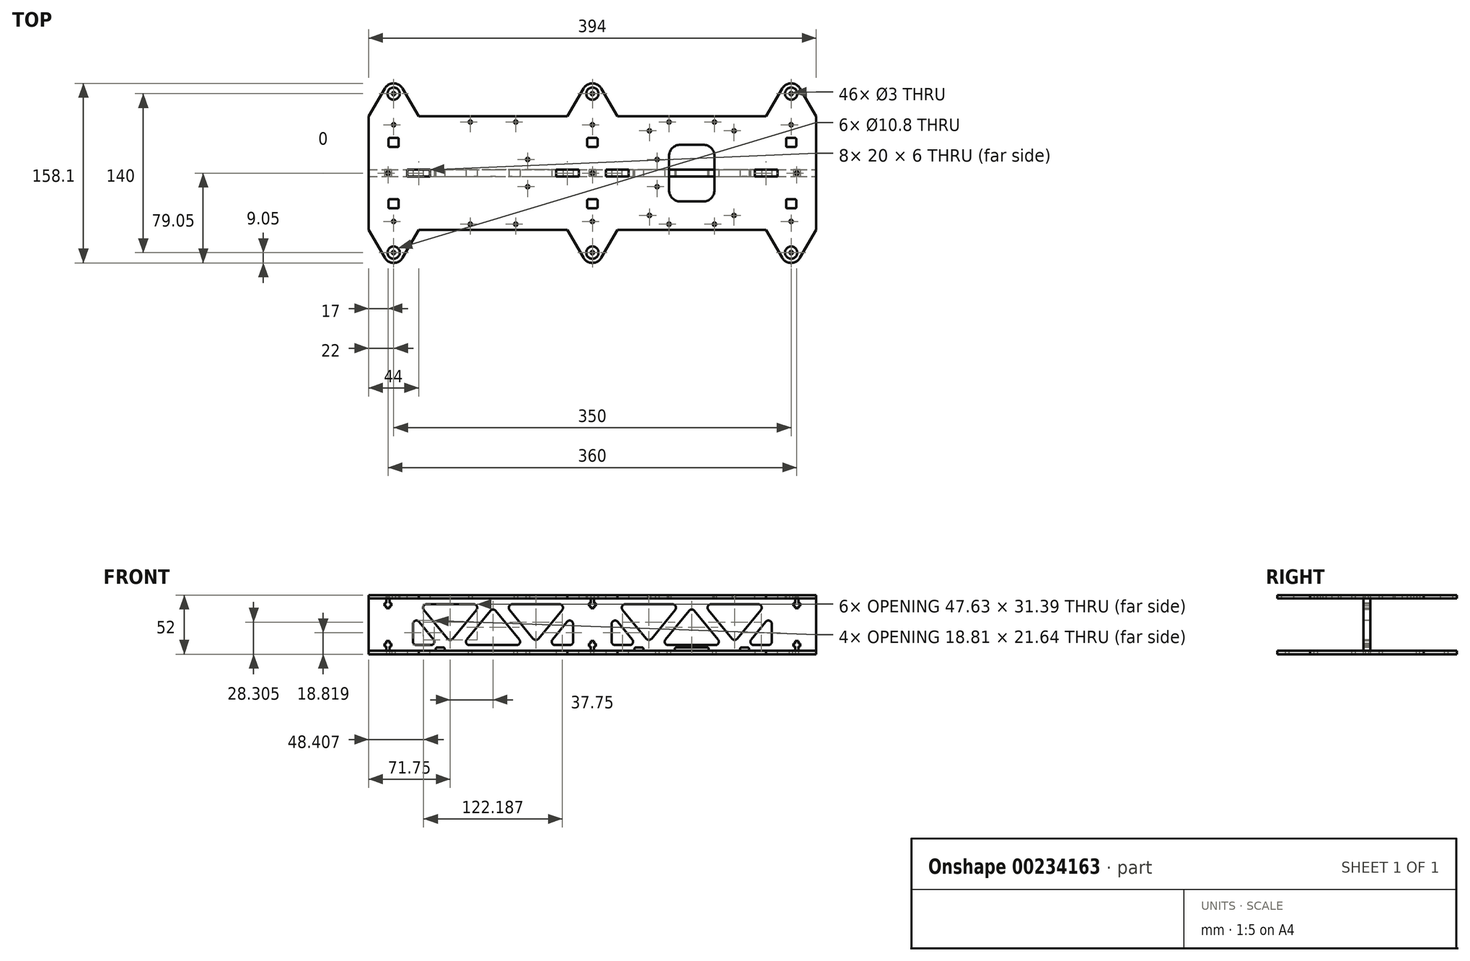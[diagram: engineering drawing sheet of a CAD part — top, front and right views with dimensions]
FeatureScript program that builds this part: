
annotation { "Feature Type Name" : "Feature", "Feature Type Description" : "" }
export const myFeature = defineFeature(function(context is Context, id is Id, definition is map)
    precondition{}
    {
        {
            assignVariable(context, id + "F0", {"name" : "MaterialThickness", "anyValue" : 3});
        }
        {
            assignVariable(context, id + "F1", {"name" : "TopBottomSeparation", "anyValue" : 46});
        }
        {
            var Q0;
            Q0=qCreatedBy(makeId("Top.planeOp"),FACE);
            var sketch = newSketch(context, id + "F2", { "sketchPlane" : qUnion([Q0])});
            skArc(sketch, "E0", {"start": v(7.84, 4.53) * mm, "mid": v(0, 9.05) * mm, "end": v(-7.84, 4.53) * mm});
            skLineSegment(sketch, "E1", {"start": v(-7.84, 4.53) * mm, "end": v(-22, -20) * mm});
            skLineSegment(sketch, "E2", {"start": v(0, 0) * mm, "end": v(0, -9.05) * mm, "construction": true});
            skLineSegment(sketch, "E3.MirrorCS", {"start": v(7.84, 4.53) * mm, "end": v(22, -20) * mm});
            skLineSegment(sketch, "E4", {"start": v(-22, -20) * mm, "end": v(-153, -20) * mm});
            skLineSegment(sketch, "E5.1.0.0", {"start": v(-167.16, 4.53) * mm, "end": v(-153, -20) * mm});
            skArc(sketch, "E5.1.0.1", {"start": v(-167.16, 4.53) * mm, "mid": v(-175, 9.05) * mm, "end": v(-182.84, 4.53) * mm});
            skLineSegment(sketch, "E5.1.0.2", {"start": v(-182.84, 4.53) * mm, "end": v(-197, -20) * mm});
            skLineSegment(sketch, "E5.2.0.0", {"start": v(-342.16, 4.53) * mm, "end": v(-328, -20) * mm});
            skArc(sketch, "E5.2.0.1", {"start": v(-342.16, 4.53) * mm, "mid": v(-350, 9.05) * mm, "end": v(-357.84, 4.53) * mm});
            skLineSegment(sketch, "E5.2.0.2", {"start": v(-357.84, 4.53) * mm, "end": v(-372, -20) * mm});
            skLineSegment(sketch, "E5.direction1", {"start": v(22, -20) * mm, "end": v(-153, -20) * mm, "construction": true});
            skLineSegment(sketch, "E6", {"start": v(-197, -20) * mm, "end": v(-328, -20) * mm});
            skLineSegment(sketch, "E7", {"start": v(22, -70) * mm, "end": v(-372, -70) * mm, "construction": true});
            skCircle(sketch, "E8", {"center": v(0, 0) * mm, "radius": 5.4 * mm});
            skCircle(sketch, "E9", {"center": v(0, -27.43) * mm, "radius": 1.5 * mm});
            skCircle(sketch, "E10.1.0.0", {"center": v(-175, 0) * mm, "radius": 5.4 * mm});
            skCircle(sketch, "E10.1.0.1", {"center": v(-175, -27.43) * mm, "radius": 1.5 * mm});
            skCircle(sketch, "E10.2.0.0", {"center": v(-350, 0) * mm, "radius": 5.4 * mm});
            skCircle(sketch, "E10.2.0.1", {"center": v(-350, -27.43) * mm, "radius": 1.5 * mm});
            skLineSegment(sketch, "E10.direction1", {"start": v(0, 0) * mm, "end": v(-175, 0) * mm, "construction": true});
            skLineSegment(sketch, "E11", {"start": v(-262.5, -70) * mm, "end": v(-262.5, -20) * mm, "construction": true});
            skLineSegment(sketch, "E12", {"start": v(-175, 0) * mm, "end": v(-175, -70) * mm, "construction": true});
            skLineSegment(sketch, "E13", {"start": v(-372, -20) * mm, "end": v(-372, -70) * mm});
            skCircle(sketch, "E14", {"center": v(-282.5, -25) * mm, "radius": 1.5 * mm});
            skCircle(sketch, "E15", {"center": v(-242.5, -25) * mm, "radius": 1.5 * mm});
            skLineSegment(sketch, "E16", {"start": v(22, -20) * mm, "end": v(22, -70) * mm});
            skCircle(sketch, "E17.MirrorC", {"center": v(-67.5, -25) * mm, "radius": 1.5 * mm});
            skCircle(sketch, "E18.MirrorC", {"center": v(-107.5, -25) * mm, "radius": 1.5 * mm});
            skLineSegment(sketch, "E19", {"start": v(0, 0) * mm, "end": v(0, -70) * mm, "construction": true});
            skLineSegment(sketch, "E20.rect.bottom", {"start": v(3.5, -47) * mm, "end": v(-3.5, -47) * mm});
            skLineSegment(sketch, "E20.rect.top", {"start": v(3.5, -39) * mm, "end": v(-3.5, -39) * mm});
            skLineSegment(sketch, "E20.rect.left", {"start": v(4.5, -46) * mm, "end": v(4.5, -40) * mm});
            skLineSegment(sketch, "E20.rect.right", {"start": v(-4.5, -46) * mm, "end": v(-4.5, -40) * mm});
            skPoint(sketch, "E20.rect.middle", {"position": v(0, -43) * mm});
            skPoint(sketch, "E21.visualSharp", {"position": v(-4.5, -39) * mm});
            skArc(sketch, "E21.filletArc", {"start": v(-3.5, -39) * mm, "mid": v(-4.2, -39.3) * mm, "end": v(-4.5, -40) * mm});
            skPoint(sketch, "E22.visualSharp", {"position": v(4.5, -39) * mm});
            skArc(sketch, "E22.filletArc", {"start": v(4.5, -40) * mm, "mid": v(4.2, -39.3) * mm, "end": v(3.5, -39) * mm});
            skPoint(sketch, "E23.visualSharp", {"position": v(-4.5, -47) * mm});
            skArc(sketch, "E23.filletArc", {"start": v(-4.5, -46) * mm, "mid": v(-4.2, -46.7) * mm, "end": v(-3.5, -47) * mm});
            skPoint(sketch, "E24.visualSharp", {"position": v(4.5, -47) * mm});
            skArc(sketch, "E24.filletArc", {"start": v(3.5, -47) * mm, "mid": v(4.2, -46.7) * mm, "end": v(4.5, -46) * mm});
            skLineSegment(sketch, "E25.1.0.0", {"start": v(-171.5, -39) * mm, "end": v(-178.5, -39) * mm});
            skPoint(sketch, "E25.1.0.1", {"position": v(-170.5, -39) * mm});
            skPoint(sketch, "E25.1.0.2", {"position": v(-175, -43) * mm});
            skLineSegment(sketch, "E25.1.0.3", {"start": v(-170.5, -46) * mm, "end": v(-170.5, -40) * mm});
            skPoint(sketch, "E25.1.0.4", {"position": v(-179.5, -47) * mm});
            skLineSegment(sketch, "E25.1.0.5", {"start": v(-171.5, -47) * mm, "end": v(-178.5, -47) * mm});
            skPoint(sketch, "E25.1.0.6", {"position": v(-170.5, -47) * mm});
            skPoint(sketch, "E25.1.0.7", {"position": v(-179.5, -39) * mm});
            skLineSegment(sketch, "E25.1.0.8", {"start": v(-179.5, -46) * mm, "end": v(-179.5, -40) * mm});
            skArc(sketch, "E25.1.0.9", {"start": v(-179.5, -46) * mm, "mid": v(-179.2, -46.7) * mm, "end": v(-178.5, -47) * mm});
            skArc(sketch, "E25.1.0.10", {"start": v(-170.5, -40) * mm, "mid": v(-170.8, -39.3) * mm, "end": v(-171.5, -39) * mm});
            skArc(sketch, "E25.1.0.11", {"start": v(-171.5, -47) * mm, "mid": v(-170.8, -46.7) * mm, "end": v(-170.5, -46) * mm});
            skArc(sketch, "E25.1.0.12", {"start": v(-178.5, -39) * mm, "mid": v(-179.2, -39.3) * mm, "end": v(-179.5, -40) * mm});
            skLineSegment(sketch, "E25.2.0.0", {"start": v(-346.5, -39) * mm, "end": v(-353.5, -39) * mm});
            skPoint(sketch, "E25.2.0.1", {"position": v(-345.5, -39) * mm});
            skPoint(sketch, "E25.2.0.2", {"position": v(-350, -43) * mm});
            skLineSegment(sketch, "E25.2.0.3", {"start": v(-345.5, -46) * mm, "end": v(-345.5, -40) * mm});
            skPoint(sketch, "E25.2.0.4", {"position": v(-354.5, -47) * mm});
            skLineSegment(sketch, "E25.2.0.5", {"start": v(-346.5, -47) * mm, "end": v(-353.5, -47) * mm});
            skPoint(sketch, "E25.2.0.6", {"position": v(-345.5, -47) * mm});
            skPoint(sketch, "E25.2.0.7", {"position": v(-354.5, -39) * mm});
            skLineSegment(sketch, "E25.2.0.8", {"start": v(-354.5, -46) * mm, "end": v(-354.5, -40) * mm});
            skArc(sketch, "E25.2.0.9", {"start": v(-354.5, -46) * mm, "mid": v(-354.2, -46.7) * mm, "end": v(-353.5, -47) * mm});
            skArc(sketch, "E25.2.0.10", {"start": v(-345.5, -40) * mm, "mid": v(-345.8, -39.3) * mm, "end": v(-346.5, -39) * mm});
            skArc(sketch, "E25.2.0.11", {"start": v(-346.5, -47) * mm, "mid": v(-345.8, -46.7) * mm, "end": v(-345.5, -46) * mm});
            skArc(sketch, "E25.2.0.12", {"start": v(-353.5, -39) * mm, "mid": v(-354.2, -39.3) * mm, "end": v(-354.5, -40) * mm});
            skLineSegment(sketch, "E25.direction1", {"start": v(-3.5, -39) * mm, "end": v(-178.5, -39) * mm, "construction": true});
            skLineSegment(sketch, "E26.MirrorCS", {"start": v(4.5, -94) * mm, "end": v(4.5, -100) * mm});
            skLineSegment(sketch, "E27.MirrorCS", {"start": v(3.5, -93) * mm, "end": v(-3.5, -93) * mm});
            skArc(sketch, "E28.MirrorCS", {"start": v(3.5, -93) * mm, "mid": v(4.2, -93.3) * mm, "end": v(4.5, -94) * mm});
            skLineSegment(sketch, "E29.MirrorCS", {"start": v(-4.5, -94) * mm, "end": v(-4.5, -100) * mm});
            skLineSegment(sketch, "E30.MirrorCS", {"start": v(-179.5, -94) * mm, "end": v(-179.5, -100) * mm});
            skLineSegment(sketch, "E31.MirrorCS", {"start": v(-171.5, -93) * mm, "end": v(-178.5, -93) * mm});
            skArc(sketch, "E32.MirrorCS", {"start": v(-179.5, -94) * mm, "mid": v(-179.2, -93.3) * mm, "end": v(-178.5, -93) * mm});
            skArc(sketch, "E33.MirrorCS", {"start": v(-171.5, -93) * mm, "mid": v(-170.8, -93.3) * mm, "end": v(-170.5, -94) * mm});
            skLineSegment(sketch, "E34.MirrorCS", {"start": v(-170.5, -94) * mm, "end": v(-170.5, -100) * mm});
            skArc(sketch, "E35.MirrorCS", {"start": v(-4.5, -94) * mm, "mid": v(-4.2, -93.3) * mm, "end": v(-3.5, -93) * mm});
            skArc(sketch, "E36.MirrorCS", {"start": v(4.5, -100) * mm, "mid": v(4.2, -100.7) * mm, "end": v(3.5, -101) * mm});
            skLineSegment(sketch, "E37.MirrorCS", {"start": v(-345.5, -94) * mm, "end": v(-345.5, -100) * mm});
            skLineSegment(sketch, "E38.MirrorCS", {"start": v(-171.5, -101) * mm, "end": v(-178.5, -101) * mm});
            skLineSegment(sketch, "E39.MirrorCS", {"start": v(3.5, -101) * mm, "end": v(-3.5, -101) * mm});
            skArc(sketch, "E40.MirrorCS", {"start": v(-178.5, -101) * mm, "mid": v(-179.2, -100.7) * mm, "end": v(-179.5, -100) * mm});
            skArc(sketch, "E41.MirrorCS", {"start": v(-3.5, -101) * mm, "mid": v(-4.2, -100.7) * mm, "end": v(-4.5, -100) * mm});
            skArc(sketch, "E42.MirrorCS", {"start": v(-170.5, -100) * mm, "mid": v(-170.8, -100.7) * mm, "end": v(-171.5, -101) * mm});
            skLineSegment(sketch, "E43.MirrorCS", {"start": v(-354.5, -94) * mm, "end": v(-354.5, -100) * mm});
            skArc(sketch, "E44.MirrorCS", {"start": v(-354.5, -94) * mm, "mid": v(-354.2, -93.3) * mm, "end": v(-353.5, -93) * mm});
            skLineSegment(sketch, "E45.MirrorCS", {"start": v(-346.5, -93) * mm, "end": v(-353.5, -93) * mm});
            skLineSegment(sketch, "E46.MirrorCS", {"start": v(-346.5, -101) * mm, "end": v(-353.5, -101) * mm});
            skArc(sketch, "E47.MirrorCS", {"start": v(-353.5, -101) * mm, "mid": v(-354.2, -100.7) * mm, "end": v(-354.5, -100) * mm});
            skArc(sketch, "E48.MirrorCS", {"start": v(-345.5, -100) * mm, "mid": v(-345.8, -100.7) * mm, "end": v(-346.5, -101) * mm});
            skCircle(sketch, "E49.MirrorC", {"center": v(-67.5, -115) * mm, "radius": 1.5 * mm});
            skCircle(sketch, "E50.MirrorC", {"center": v(-107.5, -115) * mm, "radius": 1.5 * mm});
            skCircle(sketch, "E51.MirrorC", {"center": v(0, -112.57) * mm, "radius": 1.5 * mm});
            skCircle(sketch, "E52.MirrorC", {"center": v(-282.5, -115) * mm, "radius": 1.5 * mm});
            skArc(sketch, "E53.MirrorCS", {"start": v(-342.16, -144.53) * mm, "mid": v(-350, -149.05) * mm, "end": v(-357.84, -144.53) * mm});
            skCircle(sketch, "E54.MirrorC", {"center": v(-350, -112.57) * mm, "radius": 1.5 * mm});
            skCircle(sketch, "E55.MirrorC", {"center": v(-242.5, -115) * mm, "radius": 1.5 * mm});
            skLineSegment(sketch, "E56.MirrorCS", {"start": v(0, -140) * mm, "end": v(0, -130.95) * mm, "construction": true});
            skCircle(sketch, "E57.MirrorC", {"center": v(-175, -112.57) * mm, "radius": 1.5 * mm});
            skLineSegment(sketch, "E58.MirrorCS", {"start": v(-175, -140) * mm, "end": v(-175, -70) * mm, "construction": true});
            skPoint(sketch, "E59.MirrorP", {"position": v(-179.5, -93) * mm});
            skPoint(sketch, "E60.MirrorP", {"position": v(-350, -97) * mm});
            skPoint(sketch, "E61.MirrorP", {"position": v(4.5, -93) * mm});
            skLineSegment(sketch, "E62.MirrorCS", {"start": v(-3.5, -101) * mm, "end": v(-178.5, -101) * mm, "construction": true});
            skPoint(sketch, "E63.MirrorP", {"position": v(-179.5, -101) * mm});
            skArc(sketch, "E64.MirrorCS", {"start": v(7.84, -144.53) * mm, "mid": v(0, -149.05) * mm, "end": v(-7.84, -144.53) * mm});
            skLineSegment(sketch, "E65.MirrorCS", {"start": v(-197, -120) * mm, "end": v(-328, -120) * mm});
            skPoint(sketch, "E66.MirrorP", {"position": v(-354.5, -93) * mm});
            skLineSegment(sketch, "E67.MirrorCS", {"start": v(-22, -120) * mm, "end": v(-153, -120) * mm});
            skCircle(sketch, "E68.MirrorC", {"center": v(0, -140) * mm, "radius": 5.4 * mm});
            skPoint(sketch, "E69.MirrorP", {"position": v(-4.5, -101) * mm});
            skLineSegment(sketch, "E70.MirrorCS", {"start": v(0, -140) * mm, "end": v(0, -70) * mm, "construction": true});
            skLineSegment(sketch, "E71.MirrorCS", {"start": v(-357.84, -144.53) * mm, "end": v(-372, -120) * mm});
            skLineSegment(sketch, "E72.MirrorCS", {"start": v(22, -120) * mm, "end": v(-153, -120) * mm, "construction": true});
            skCircle(sketch, "E73.MirrorC", {"center": v(-175, -140) * mm, "radius": 5.4 * mm});
            skPoint(sketch, "E74.MirrorP", {"position": v(-354.5, -101) * mm});
            skLineSegment(sketch, "E75.MirrorCS", {"start": v(7.84, -144.53) * mm, "end": v(22, -120) * mm});
            skLineSegment(sketch, "E76.MirrorCS", {"start": v(-372, -120) * mm, "end": v(-372, -70) * mm});
            skPoint(sketch, "E77.MirrorP", {"position": v(-175, -97) * mm});
            skPoint(sketch, "E78.MirrorP", {"position": v(4.5, -101) * mm});
            skArc(sketch, "E79.MirrorCS", {"start": v(-167.16, -144.53) * mm, "mid": v(-175, -149.05) * mm, "end": v(-182.84, -144.53) * mm});
            skPoint(sketch, "E80.MirrorP", {"position": v(0, -97) * mm});
            skLineSegment(sketch, "E81.MirrorCS", {"start": v(-7.84, -144.53) * mm, "end": v(-22, -120) * mm});
            skLineSegment(sketch, "E82.MirrorCS", {"start": v(-262.5, -70) * mm, "end": v(-262.5, -120) * mm, "construction": true});
            skLineSegment(sketch, "E83.MirrorCS", {"start": v(-167.16, -144.53) * mm, "end": v(-153, -120) * mm});
            skLineSegment(sketch, "E84.MirrorCS", {"start": v(-182.84, -144.53) * mm, "end": v(-197, -120) * mm});
            skLineSegment(sketch, "E85.MirrorCS", {"start": v(-342.16, -144.53) * mm, "end": v(-328, -120) * mm});
            skPoint(sketch, "E86.MirrorP", {"position": v(-170.5, -93) * mm});
            skPoint(sketch, "E87.MirrorP", {"position": v(-345.5, -93) * mm});
            skPoint(sketch, "E88.MirrorP", {"position": v(-345.5, -101) * mm});
            skPoint(sketch, "E89.MirrorP", {"position": v(-4.5, -93) * mm});
            skLineSegment(sketch, "E90.MirrorCS", {"start": v(22, -120) * mm, "end": v(22, -70) * mm});
            skPoint(sketch, "E91.MirrorP", {"position": v(-170.5, -101) * mm});
            skLineSegment(sketch, "E92.MirrorCS", {"start": v(0, -140) * mm, "end": v(-175, -140) * mm, "construction": true});
            skCircle(sketch, "E93.MirrorC", {"center": v(-350, -140) * mm, "radius": 5.4 * mm});
            skArc(sketch, "E94.MirrorCS", {"start": v(-346.5, -93) * mm, "mid": v(-345.8, -93.3) * mm, "end": v(-345.5, -94) * mm});
            skSolve(sketch);
        }
        {
            var Q0;
            Q0=makeQuery(id+"F2.imprint","IMPRINT",FACE,{"disambiguationData":[TD([[makeQuery(id+"F2.imprint","IMPRINT",EDGE,{"derivedFrom":sQuery(id+"F2.wireOp",EDGE,"E0")}),1.0]])]});
            extrude(context, id + "F3", {"entities" : qUnion([Q0]), "depth" : (getVariable(context, 'MaterialThickness')) * mm});
        }
        {
            var Q0;
            Q0=makeQuery(id+"F3.opExtrude","CAP_FACE",FACE,{"disambiguationData":[OSD([sQuery(id+"F2.wireOp",EDGE,"E0"),sQuery(id+"F2.wireOp",EDGE,"E1"),sQuery(id+"F2.wireOp",EDGE,"E3.MirrorCS"),sQuery(id+"F2.wireOp",EDGE,"E4"),sQuery(id+"F2.wireOp",EDGE,"E5.1.0.0"),sQuery(id+"F2.wireOp",EDGE,"E5.1.0.1"),sQuery(id+"F2.wireOp",EDGE,"E5.1.0.2"),sQuery(id+"F2.wireOp",EDGE,"E5.2.0.0"),sQuery(id+"F2.wireOp",EDGE,"E5.2.0.2"),sQuery(id+"F2.wireOp",EDGE,"E6"),sQuery(id+"F2.wireOp",EDGE,"E8"),sQuery(id+"F2.wireOp",EDGE,"E9"),sQuery(id+"F2.wireOp",EDGE,"E10.1.0.0"),sQuery(id+"F2.wireOp",EDGE,"E10.1.0.1"),sQuery(id+"F2.wireOp",EDGE,"E5.2.0.1"),sQuery(id+"F2.wireOp",EDGE,"E10.2.0.0"),sQuery(id+"F2.wireOp",EDGE,"E10.2.0.1"),sQuery(id+"F2.wireOp",EDGE,"E13"),sQuery(id+"F2.wireOp",EDGE,"E14"),sQuery(id+"F2.wireOp",EDGE,"E15"),sQuery(id+"F2.wireOp",EDGE,"E16"),sQuery(id+"F2.wireOp",EDGE,"E18.MirrorC"),sQuery(id+"F2.wireOp",EDGE,"E17.MirrorC"),sQuery(id+"F2.wireOp",EDGE,"E20.rect.bottom"),sQuery(id+"F2.wireOp",EDGE,"E20.rect.top"),sQuery(id+"F2.wireOp",EDGE,"E20.rect.left"),sQuery(id+"F2.wireOp",EDGE,"E20.rect.right"),sQuery(id+"F2.wireOp",EDGE,"E21.filletArc"),sQuery(id+"F2.wireOp",EDGE,"E22.filletArc"),sQuery(id+"F2.wireOp",EDGE,"E23.filletArc"),sQuery(id+"F2.wireOp",EDGE,"E24.filletArc"),sQuery(id+"F2.wireOp",EDGE,"E25.1.0.0"),sQuery(id+"F2.wireOp",EDGE,"E25.1.0.3"),sQuery(id+"F2.wireOp",EDGE,"E25.1.0.5"),sQuery(id+"F2.wireOp",EDGE,"E25.1.0.8"),sQuery(id+"F2.wireOp",EDGE,"E25.1.0.9"),sQuery(id+"F2.wireOp",EDGE,"E25.1.0.10"),sQuery(id+"F2.wireOp",EDGE,"E25.1.0.11"),sQuery(id+"F2.wireOp",EDGE,"E25.1.0.12"),sQuery(id+"F2.wireOp",EDGE,"E25.2.0.0"),sQuery(id+"F2.wireOp",EDGE,"E25.2.0.3"),sQuery(id+"F2.wireOp",EDGE,"E25.2.0.5"),sQuery(id+"F2.wireOp",EDGE,"E25.2.0.8"),sQuery(id+"F2.wireOp",EDGE,"E25.2.0.9"),sQuery(id+"F2.wireOp",EDGE,"E25.2.0.10"),sQuery(id+"F2.wireOp",EDGE,"E25.2.0.11"),sQuery(id+"F2.wireOp",EDGE,"E25.2.0.12"),sQuery(id+"F2.wireOp",EDGE,"E26.MirrorCS"),sQuery(id+"F2.wireOp",EDGE,"E27.MirrorCS"),sQuery(id+"F2.wireOp",EDGE,"E28.MirrorCS"),sQuery(id+"F2.wireOp",EDGE,"E29.MirrorCS"),sQuery(id+"F2.wireOp",EDGE,"E30.MirrorCS"),sQuery(id+"F2.wireOp",EDGE,"E31.MirrorCS"),sQuery(id+"F2.wireOp",EDGE,"E32.MirrorCS"),sQuery(id+"F2.wireOp",EDGE,"E33.MirrorCS"),sQuery(id+"F2.wireOp",EDGE,"E34.MirrorCS"),sQuery(id+"F2.wireOp",EDGE,"E35.MirrorCS"),sQuery(id+"F2.wireOp",EDGE,"E36.MirrorCS"),sQuery(id+"F2.wireOp",EDGE,"E37.MirrorCS"),sQuery(id+"F2.wireOp",EDGE,"E38.MirrorCS"),sQuery(id+"F2.wireOp",EDGE,"E39.MirrorCS"),sQuery(id+"F2.wireOp",EDGE,"E40.MirrorCS"),sQuery(id+"F2.wireOp",EDGE,"E41.MirrorCS"),sQuery(id+"F2.wireOp",EDGE,"E42.MirrorCS"),sQuery(id+"F2.wireOp",EDGE,"E43.MirrorCS"),sQuery(id+"F2.wireOp",EDGE,"E44.MirrorCS"),sQuery(id+"F2.wireOp",EDGE,"E45.MirrorCS"),sQuery(id+"F2.wireOp",EDGE,"E46.MirrorCS"),sQuery(id+"F2.wireOp",EDGE,"E47.MirrorCS"),sQuery(id+"F2.wireOp",EDGE,"E48.MirrorCS"),sQuery(id+"F2.wireOp",EDGE,"E49.MirrorC"),sQuery(id+"F2.wireOp",EDGE,"E50.MirrorC"),sQuery(id+"F2.wireOp",EDGE,"E51.MirrorC"),sQuery(id+"F2.wireOp",EDGE,"E52.MirrorC"),sQuery(id+"F2.wireOp",EDGE,"E54.MirrorC"),sQuery(id+"F2.wireOp",EDGE,"E55.MirrorC"),sQuery(id+"F2.wireOp",EDGE,"E57.MirrorC"),sQuery(id+"F2.wireOp",EDGE,"E64.MirrorCS"),sQuery(id+"F2.wireOp",EDGE,"E65.MirrorCS"),sQuery(id+"F2.wireOp",EDGE,"E67.MirrorCS"),sQuery(id+"F2.wireOp",EDGE,"E68.MirrorC"),sQuery(id+"F2.wireOp",EDGE,"E71.MirrorCS"),sQuery(id+"F2.wireOp",EDGE,"E73.MirrorC"),sQuery(id+"F2.wireOp",EDGE,"E75.MirrorCS"),sQuery(id+"F2.wireOp",EDGE,"E76.MirrorCS"),sQuery(id+"F2.wireOp",EDGE,"E79.MirrorCS"),sQuery(id+"F2.wireOp",EDGE,"E81.MirrorCS"),sQuery(id+"F2.wireOp",EDGE,"E83.MirrorCS"),sQuery(id+"F2.wireOp",EDGE,"E84.MirrorCS"),sQuery(id+"F2.wireOp",EDGE,"E53.MirrorCS"),sQuery(id+"F2.wireOp",EDGE,"E85.MirrorCS"),sQuery(id+"F2.wireOp",EDGE,"E90.MirrorCS"),sQuery(id+"F2.wireOp",EDGE,"E93.MirrorC"),sQuery(id+"F2.wireOp",EDGE,"E94.MirrorCS")])],"isStart":true});
            cPlane(context, id + "F4", {"entities" : qUnion([Q0]), "cplaneType" : CPlaneType.OFFSET, "offset" : (getVariable(context, 'TopBottomSeparation')) * mm, "width" : 150 * mm, "height" : 150 * mm});
        }
        {
            var Q0;
            Q0=qCreatedBy(id+"F4.planeOp",FACE);
            var sketch = newSketch(context, id + "F5", { "sketchPlane" : qUnion([Q0])});
            skLineSegment(sketch, "E95.0", {"start": v(-357.84, -4.53) * mm, "end": v(-357.84, -4.53) * mm});
            skLineSegment(sketch, "E96.0", {"start": v(7.84, -4.53) * mm, "end": v(22, 20) * mm});
            skLineSegment(sketch, "E97.0", {"start": v(-7.84, -4.53) * mm, "end": v(-22, 20) * mm});
            skArc(sketch, "E98.0", {"start": v(7.84, -4.53) * mm, "mid": v(0, -9.05) * mm, "end": v(-7.84, -4.53) * mm});
            skLineSegment(sketch, "E99.0", {"start": v(-22, 20) * mm, "end": v(-153, 20) * mm});
            skLineSegment(sketch, "E100.0", {"start": v(-167.16, -4.53) * mm, "end": v(-153, 20) * mm});
            skArc(sketch, "E101.0", {"start": v(-167.16, -4.53) * mm, "mid": v(-175, -9.05) * mm, "end": v(-182.84, -4.53) * mm});
            skLineSegment(sketch, "E102.0", {"start": v(-182.84, -4.53) * mm, "end": v(-197, 20) * mm});
            skLineSegment(sketch, "E103.0", {"start": v(-197, 20) * mm, "end": v(-328, 20) * mm});
            skLineSegment(sketch, "E104.0", {"start": v(-342.16, -4.53) * mm, "end": v(-328, 20) * mm});
            skArc(sketch, "E105.0", {"start": v(-342.16, -4.53) * mm, "mid": v(-350, -9.05) * mm, "end": v(-357.84, -4.53) * mm});
            skCircle(sketch, "E106", {"center": v(-350, 0) * mm, "radius": 1.5 * mm});
            skCircle(sketch, "E107.1.0.0", {"center": v(-175, 0) * mm, "radius": 1.5 * mm});
            skCircle(sketch, "E107.2.0.0", {"center": v(0, 0) * mm, "radius": 1.5 * mm});
            skLineSegment(sketch, "E107.direction1", {"start": v(-350, 0) * mm, "end": v(-175, 0) * mm, "construction": true});
            skLineSegment(sketch, "E108", {"start": v(-372, 70) * mm, "end": v(22, 70) * mm, "construction": true});
            skLineSegment(sketch, "E109.0", {"start": v(-357.84, -4.53) * mm, "end": v(-372, 20) * mm});
            skLineSegment(sketch, "E110.0", {"start": v(-372, 20) * mm, "end": v(-372, 120) * mm});
            skLineSegment(sketch, "E111.0", {"start": v(22, 120) * mm, "end": v(22, 20) * mm});
            skCircle(sketch, "E112.0", {"center": v(-282.5, 25) * mm, "radius": 1.5 * mm});
            skCircle(sketch, "E112.1", {"center": v(-242.5, 25) * mm, "radius": 1.5 * mm});
            skCircle(sketch, "E112.2", {"center": v(-107.5, 25) * mm, "radius": 1.5 * mm});
            skCircle(sketch, "E112.3", {"center": v(-67.5, 25) * mm, "radius": 1.5 * mm});
            skCircle(sketch, "E113.MirrorC", {"center": v(-350, 140) * mm, "radius": 1.5 * mm});
            skCircle(sketch, "E114.MirrorC", {"center": v(-175, 140) * mm, "radius": 1.5 * mm});
            skCircle(sketch, "E115.MirrorC", {"center": v(0, 140) * mm, "radius": 1.5 * mm});
            skCircle(sketch, "E116.MirrorC", {"center": v(-282.5, 115) * mm, "radius": 1.5 * mm});
            skCircle(sketch, "E117.MirrorC", {"center": v(-242.5, 115) * mm, "radius": 1.5 * mm});
            skCircle(sketch, "E118.MirrorC", {"center": v(-107.5, 115) * mm, "radius": 1.5 * mm});
            skCircle(sketch, "E119.MirrorC", {"center": v(-67.5, 115) * mm, "radius": 1.5 * mm});
            skArc(sketch, "E120.MirrorCS", {"start": v(-167.16, 144.53) * mm, "mid": v(-175, 149.05) * mm, "end": v(-182.84, 144.53) * mm});
            skLineSegment(sketch, "E121.MirrorCS", {"start": v(-357.84, 144.53) * mm, "end": v(-357.84, 144.53) * mm});
            skLineSegment(sketch, "E122.MirrorCS", {"start": v(-357.84, 144.53) * mm, "end": v(-372, 120) * mm});
            skLineSegment(sketch, "E123.MirrorCS", {"start": v(7.84, 144.53) * mm, "end": v(22, 120) * mm});
            skArc(sketch, "E124.MirrorCS", {"start": v(-342.16, 144.53) * mm, "mid": v(-350, 149.05) * mm, "end": v(-357.84, 144.53) * mm});
            skLineSegment(sketch, "E125.MirrorCS", {"start": v(-7.84, 144.53) * mm, "end": v(-22, 120) * mm});
            skArc(sketch, "E126.MirrorCS", {"start": v(7.84, 144.53) * mm, "mid": v(0, 149.05) * mm, "end": v(-7.84, 144.53) * mm});
            skLineSegment(sketch, "E127.MirrorCS", {"start": v(-342.16, 144.53) * mm, "end": v(-328, 120) * mm});
            skLineSegment(sketch, "E128.MirrorCS", {"start": v(-197, 120) * mm, "end": v(-328, 120) * mm});
            skLineSegment(sketch, "E129.MirrorCS", {"start": v(-182.84, 144.53) * mm, "end": v(-197, 120) * mm});
            skLineSegment(sketch, "E130.MirrorCS", {"start": v(-167.16, 144.53) * mm, "end": v(-153, 120) * mm});
            skLineSegment(sketch, "E131.MirrorCS", {"start": v(-350, 140) * mm, "end": v(-175, 140) * mm, "construction": true});
            skLineSegment(sketch, "E132.MirrorCS", {"start": v(-22, 120) * mm, "end": v(-153, 120) * mm});
            skSolve(sketch);
        }
        {
            var Q0;
            Q0=qSketchRegion(id+"F5",true);
            extrude(context, id + "F6", {"entities" : qUnion([Q0]), "depth" : (getVariable(context, 'MaterialThickness')) * mm});
        }
        {
            var Q0;
            Q0=makeQuery(id+"F3.opExtrude","CAP_FACE",FACE,{"disambiguationData":[OSD([sQuery(id+"F0T68XCoUrNjqKc_0.merge.FRI3efolS22JnH9_0.merge.F2le2PEO98lg6xs_0.merge.FXX2dDxdAnKxtOb_1.wireOp",EDGE,"a45bbf6a-1b3a-4c73-aa77-97d7b8075cbb"),sQuery(id+"F2.wireOp",EDGE,"E0"),sQuery(id+"F2.wireOp",EDGE,"E1"),sQuery(id+"F2.wireOp",EDGE,"E3.MirrorCS"),sQuery(id+"F2.wireOp",EDGE,"E4"),sQuery(id+"F2.wireOp",EDGE,"E5.1.0.0"),sQuery(id+"F2.wireOp",EDGE,"E5.1.0.1"),sQuery(id+"F2.wireOp",EDGE,"E5.1.0.2"),sQuery(id+"F2.wireOp",EDGE,"E5.2.0.0"),sQuery(id+"F2.wireOp",EDGE,"E5.2.0.2"),sQuery(id+"F2.wireOp",EDGE,"E6"),sQuery(id+"F2.wireOp",EDGE,"E9"),sQuery(id+"F2.wireOp",EDGE,"E10.1.0.0"),sQuery(id+"F2.wireOp",EDGE,"E10.1.0.1"),sQuery(id+"F2.wireOp",EDGE,"E5.2.0.1"),sQuery(id+"F2.wireOp",EDGE,"E10.2.0.0"),sQuery(id+"F2.wireOp",EDGE,"E10.2.0.1"),sQuery(id+"F2.wireOp",EDGE,"E13"),sQuery(id+"F2.wireOp",EDGE,"E14"),sQuery(id+"F2.wireOp",EDGE,"E15"),sQuery(id+"F2.wireOp",EDGE,"E16"),sQuery(id+"F2.wireOp",EDGE,"E18.MirrorC"),sQuery(id+"F2.wireOp",EDGE,"E17.MirrorC"),sQuery(id+"F2.wireOp",EDGE,"E20.rect.bottom"),sQuery(id+"F2.wireOp",EDGE,"E20.rect.top"),sQuery(id+"F2.wireOp",EDGE,"E20.rect.left"),sQuery(id+"F2.wireOp",EDGE,"E20.rect.right"),sQuery(id+"F2.wireOp",EDGE,"E21.filletArc"),sQuery(id+"F2.wireOp",EDGE,"E22.filletArc"),sQuery(id+"F2.wireOp",EDGE,"E23.filletArc"),sQuery(id+"F2.wireOp",EDGE,"E24.filletArc"),sQuery(id+"F2.wireOp",EDGE,"E25.1.0.0"),sQuery(id+"F2.wireOp",EDGE,"E25.1.0.3"),sQuery(id+"F2.wireOp",EDGE,"E25.1.0.5"),sQuery(id+"F2.wireOp",EDGE,"E25.1.0.8"),sQuery(id+"F2.wireOp",EDGE,"E25.1.0.9"),sQuery(id+"F2.wireOp",EDGE,"E25.1.0.10"),sQuery(id+"F2.wireOp",EDGE,"E25.1.0.11"),sQuery(id+"F2.wireOp",EDGE,"E25.1.0.12"),sQuery(id+"F2.wireOp",EDGE,"E25.2.0.0"),sQuery(id+"F2.wireOp",EDGE,"E25.2.0.3"),sQuery(id+"F2.wireOp",EDGE,"E25.2.0.5"),sQuery(id+"F2.wireOp",EDGE,"E25.2.0.8"),sQuery(id+"F2.wireOp",EDGE,"E25.2.0.9"),sQuery(id+"F2.wireOp",EDGE,"E25.2.0.10"),sQuery(id+"F2.wireOp",EDGE,"E25.2.0.11"),sQuery(id+"F2.wireOp",EDGE,"E25.2.0.12"),sQuery(id+"F2.wireOp",EDGE,"E26.MirrorCS"),sQuery(id+"F2.wireOp",EDGE,"E27.MirrorCS"),sQuery(id+"F2.wireOp",EDGE,"E28.MirrorCS"),sQuery(id+"F2.wireOp",EDGE,"E29.MirrorCS"),sQuery(id+"F2.wireOp",EDGE,"E30.MirrorCS"),sQuery(id+"F2.wireOp",EDGE,"E31.MirrorCS"),sQuery(id+"F2.wireOp",EDGE,"E32.MirrorCS"),sQuery(id+"F2.wireOp",EDGE,"E33.MirrorCS"),sQuery(id+"F2.wireOp",EDGE,"E34.MirrorCS"),sQuery(id+"F2.wireOp",EDGE,"E35.MirrorCS"),sQuery(id+"F2.wireOp",EDGE,"E36.MirrorCS"),sQuery(id+"F2.wireOp",EDGE,"E37.MirrorCS"),sQuery(id+"F2.wireOp",EDGE,"E38.MirrorCS"),sQuery(id+"F2.wireOp",EDGE,"E39.MirrorCS"),sQuery(id+"F2.wireOp",EDGE,"E40.MirrorCS"),sQuery(id+"F2.wireOp",EDGE,"E41.MirrorCS"),sQuery(id+"F2.wireOp",EDGE,"E42.MirrorCS"),sQuery(id+"F2.wireOp",EDGE,"E43.MirrorCS"),sQuery(id+"F2.wireOp",EDGE,"E44.MirrorCS"),sQuery(id+"F2.wireOp",EDGE,"E45.MirrorCS"),sQuery(id+"F2.wireOp",EDGE,"E46.MirrorCS"),sQuery(id+"F2.wireOp",EDGE,"E47.MirrorCS"),sQuery(id+"F2.wireOp",EDGE,"E48.MirrorCS"),sQuery(id+"F2.wireOp",EDGE,"E49.MirrorC"),sQuery(id+"F2.wireOp",EDGE,"E50.MirrorC"),sQuery(id+"F2.wireOp",EDGE,"E51.MirrorC"),sQuery(id+"F2.wireOp",EDGE,"E52.MirrorC"),sQuery(id+"F2.wireOp",EDGE,"E54.MirrorC"),sQuery(id+"F2.wireOp",EDGE,"E55.MirrorC"),sQuery(id+"F2.wireOp",EDGE,"E57.MirrorC"),sQuery(id+"F2.wireOp",EDGE,"E64.MirrorCS"),sQuery(id+"F2.wireOp",EDGE,"E65.MirrorCS"),sQuery(id+"F2.wireOp",EDGE,"E67.MirrorCS"),sQuery(id+"F2.wireOp",EDGE,"E68.MirrorC"),sQuery(id+"F2.wireOp",EDGE,"E71.MirrorCS"),sQuery(id+"F2.wireOp",EDGE,"E73.MirrorC"),sQuery(id+"F2.wireOp",EDGE,"E75.MirrorCS"),sQuery(id+"F2.wireOp",EDGE,"E76.MirrorCS"),sQuery(id+"F2.wireOp",EDGE,"E79.MirrorCS"),sQuery(id+"F2.wireOp",EDGE,"E81.MirrorCS"),sQuery(id+"F2.wireOp",EDGE,"E83.MirrorCS"),sQuery(id+"F2.wireOp",EDGE,"E84.MirrorCS"),sQuery(id+"F2.wireOp",EDGE,"E53.MirrorCS"),sQuery(id+"F2.wireOp",EDGE,"E85.MirrorCS"),sQuery(id+"F2.wireOp",EDGE,"E90.MirrorCS"),sQuery(id+"F2.wireOp",EDGE,"E93.MirrorC"),sQuery(id+"F2.wireOp",EDGE,"E94.MirrorCS")])],"isStart":false});
            var sketch = newSketch(context, id + "F7", { "sketchPlane" : qUnion([Q0])});
            skLineSegment(sketch, "E133.bottom", {"start": v(-121.75, -32.75) * mm, "end": v(-53.25, -32.75) * mm, "construction": true});
            skLineSegment(sketch, "E133.top", {"start": v(-121.75, -107.25) * mm, "end": v(-53.25, -107.25) * mm, "construction": true});
            skLineSegment(sketch, "E133.left", {"start": v(-124.75, -35.75) * mm, "end": v(-124.75, -104.25) * mm, "construction": true});
            skLineSegment(sketch, "E133.right", {"start": v(-50.25, -35.75) * mm, "end": v(-50.25, -104.25) * mm, "construction": true});
            skLineSegment(sketch, "E134", {"start": v(-124.75, -70) * mm, "end": v(-50.25, -70) * mm, "construction": true});
            skLineSegment(sketch, "E135", {"start": v(-87.5, -32.75) * mm, "end": v(-87.5, -107.25) * mm, "construction": true});
            skPoint(sketch, "E136.visualSharp", {"position": v(-124.75, -32.75) * mm});
            skArc(sketch, "E136.filletArc", {"start": v(-121.75, -32.75) * mm, "mid": v(-123.87, -33.63) * mm, "end": v(-124.75, -35.75) * mm, "construction": true});
            skPoint(sketch, "E137.visualSharp", {"position": v(-50.25, -32.75) * mm});
            skArc(sketch, "E137.filletArc", {"start": v(-50.25, -35.75) * mm, "mid": v(-51.13, -33.63) * mm, "end": v(-53.25, -32.75) * mm, "construction": true});
            skPoint(sketch, "E138.visualSharp", {"position": v(-124.75, -107.25) * mm});
            skArc(sketch, "E138.filletArc", {"start": v(-124.75, -104.25) * mm, "mid": v(-123.87, -106.37) * mm, "end": v(-121.75, -107.25) * mm, "construction": true});
            skPoint(sketch, "E139.visualSharp", {"position": v(-50.25, -107.25) * mm});
            skArc(sketch, "E139.filletArc", {"start": v(-53.25, -107.25) * mm, "mid": v(-51.13, -106.37) * mm, "end": v(-50.25, -104.25) * mm, "construction": true});
            skCircle(sketch, "E140", {"center": v(-124.75, -32.75) * mm, "radius": 1.5 * mm});
            skCircle(sketch, "E141", {"center": v(-50.25, -32.75) * mm, "radius": 1.5 * mm});
            skCircle(sketch, "E142", {"center": v(-50.25, -107.25) * mm, "radius": 1.5 * mm});
            skCircle(sketch, "E143", {"center": v(-124.75, -107.25) * mm, "radius": 1.5 * mm});
            skSolve(sketch);
        }
        {
            var Q0;
            Q0=qSketchRegion(id+"F7",true);
            extrude(context, id + "F8", {"entities" : qUnion([Q0]), "operationType" : NewBodyOperationType.REMOVE, "endBound" : BoundingType.UP_TO_NEXT, "oppositeDirection" : true, "depth" : 22.5 * mm});
        }
        {
            var Q0;
            Q0=sQuery(id+"F5.wireOp",EDGE,"E108");
            cPlane(context, id + "F9", {"entities" : qUnion([Q0]), "cplaneType" : CPlaneType.LINE_ANGLE, "offset" : 150 * mm, "angle" : 0 * degree, "width" : 150 * mm, "height" : 150 * mm});
        }
        {
            var Q0;
            Q0=qCreatedBy(id+"F9.planeOp",FACE);
            var sketch = newSketch(context, id + "F10", { "sketchPlane" : qUnion([Q0])});
            skPoint(sketch, "E144", {"position": v(372, -46) * mm});
            skPoint(sketch, "E145", {"position": v(-22, -46) * mm});
            skLineSegment(sketch, "E146", {"start": v(372, -23) * mm, "end": v(-22, -23) * mm, "construction": true});
            skLineSegment(sketch, "E147", {"start": v(372, -23) * mm, "end": v(372, -46) * mm});
            skLineSegment(sketch, "E148", {"start": v(-22, -23) * mm, "end": v(-22, -46) * mm});
            skLineSegment(sketch, "E149", {"start": v(355, -46) * mm, "end": v(355, -23) * mm, "construction": true});
            skLineSegment(sketch, "E150.top", {"start": v(353.5, -37.5) * mm, "end": v(356.5, -37.5) * mm});
            skLineSegment(sketch, "E150.left", {"start": v(353.5, -46) * mm, "end": v(353.5, -42) * mm});
            skLineSegment(sketch, "E150.right", {"start": v(356.5, -46) * mm, "end": v(356.5, -42) * mm});
            skPoint(sketch, "E150.middle", {"position": v(355, -40.75) * mm});
            skLineSegment(sketch, "E151.bottom", {"start": v(352, -42) * mm, "end": v(353.5, -42) * mm});
            skLineSegment(sketch, "E151.top", {"start": v(352, -39.5) * mm, "end": v(353.5, -39.5) * mm});
            skLineSegment(sketch, "E151.left", {"start": v(352, -42) * mm, "end": v(352, -39.5) * mm});
            skLineSegment(sketch, "E151.right", {"start": v(358, -42) * mm, "end": v(358, -39.5) * mm});
            skLineSegment(sketch, "E152.trimOffspring", {"start": v(356.5, -42) * mm, "end": v(358, -42) * mm});
            skLineSegment(sketch, "E153.trimOffspring", {"start": v(353.5, -39.5) * mm, "end": v(353.5, -37.5) * mm});
            skLineSegment(sketch, "E154.trimOffspring", {"start": v(356.5, -39.5) * mm, "end": v(358, -39.5) * mm});
            skLineSegment(sketch, "E155.trimOffspring", {"start": v(356.5, -39.5) * mm, "end": v(356.5, -37.5) * mm});
            skLineSegment(sketch, "E156", {"start": v(372, -46) * mm, "end": v(356.5, -46) * mm});
            skLineSegment(sketch, "E157", {"start": v(353.5, -46) * mm, "end": v(338, -46) * mm});
            skLineSegment(sketch, "E158.0", {"start": v(328, -49) * mm, "end": v(328, -46) * mm, "construction": true});
            skLineSegment(sketch, "E159", {"start": v(338, -46) * mm, "end": v(338, -49) * mm});
            skLineSegment(sketch, "E160", {"start": v(338, -49) * mm, "end": v(318, -49) * mm});
            skLineSegment(sketch, "E161", {"start": v(318, -49) * mm, "end": v(318, -46) * mm});
            skLineSegment(sketch, "E162.0", {"start": v(197, -49) * mm, "end": v(197, -46) * mm, "construction": true});
            skLineSegment(sketch, "E163.0", {"start": v(153, -49) * mm, "end": v(153, -46) * mm, "construction": true});
            skLineSegment(sketch, "E164.0", {"start": v(22, -49) * mm, "end": v(22, -46) * mm, "construction": true});
            skLineSegment(sketch, "E165", {"start": v(207, -46) * mm, "end": v(207, -49) * mm});
            skLineSegment(sketch, "E166", {"start": v(207, -49) * mm, "end": v(187, -49) * mm});
            skLineSegment(sketch, "E167", {"start": v(187, -49) * mm, "end": v(187, -46) * mm});
            skLineSegment(sketch, "E168", {"start": v(163, -46) * mm, "end": v(163, -49) * mm});
            skLineSegment(sketch, "E169", {"start": v(163, -49) * mm, "end": v(143, -49) * mm});
            skLineSegment(sketch, "E170", {"start": v(143, -49) * mm, "end": v(143, -46) * mm});
            skLineSegment(sketch, "E171", {"start": v(32, -46) * mm, "end": v(32, -49) * mm});
            skLineSegment(sketch, "E172", {"start": v(32, -49) * mm, "end": v(12, -49) * mm});
            skLineSegment(sketch, "E173", {"start": v(12, -49) * mm, "end": v(12, -46) * mm});
            skLineSegment(sketch, "E174.1.0.0", {"start": v(176.5, -39.5) * mm, "end": v(176.5, -37.5) * mm});
            skLineSegment(sketch, "E174.1.0.1", {"start": v(172, -42) * mm, "end": v(172, -39.5) * mm});
            skPoint(sketch, "E174.1.0.2", {"position": v(175, -40.75) * mm});
            skLineSegment(sketch, "E174.1.0.3", {"start": v(176.5, -42) * mm, "end": v(178, -42) * mm});
            skLineSegment(sketch, "E174.1.0.4", {"start": v(172, -39.5) * mm, "end": v(173.5, -39.5) * mm});
            skLineSegment(sketch, "E174.1.0.5", {"start": v(172, -42) * mm, "end": v(173.5, -42) * mm});
            skLineSegment(sketch, "E174.1.0.6", {"start": v(176.5, -46) * mm, "end": v(176.5, -42) * mm});
            skLineSegment(sketch, "E174.1.0.7", {"start": v(173.5, -37.5) * mm, "end": v(176.5, -37.5) * mm});
            skLineSegment(sketch, "E174.1.0.8", {"start": v(178, -42) * mm, "end": v(178, -39.5) * mm});
            skLineSegment(sketch, "E174.1.0.9", {"start": v(173.5, -39.5) * mm, "end": v(173.5, -37.5) * mm});
            skLineSegment(sketch, "E174.1.0.10", {"start": v(173.5, -46) * mm, "end": v(173.5, -42) * mm});
            skLineSegment(sketch, "E174.1.0.11", {"start": v(176.5, -39.5) * mm, "end": v(178, -39.5) * mm});
            skLineSegment(sketch, "E174.1.0.12", {"start": v(175, -46) * mm, "end": v(175, -23) * mm, "construction": true});
            skLineSegment(sketch, "E174.2.0.0", {"start": v(-3.5, -39.5) * mm, "end": v(-3.5, -37.5) * mm});
            skLineSegment(sketch, "E174.2.0.1", {"start": v(-8, -42) * mm, "end": v(-8, -39.5) * mm});
            skPoint(sketch, "E174.2.0.2", {"position": v(-5, -40.75) * mm});
            skLineSegment(sketch, "E174.2.0.3", {"start": v(-3.5, -42) * mm, "end": v(-2, -42) * mm});
            skLineSegment(sketch, "E174.2.0.4", {"start": v(-8, -39.5) * mm, "end": v(-6.5, -39.5) * mm});
            skLineSegment(sketch, "E174.2.0.5", {"start": v(-8, -42) * mm, "end": v(-6.5, -42) * mm});
            skLineSegment(sketch, "E174.2.0.6", {"start": v(-3.5, -46) * mm, "end": v(-3.5, -42) * mm});
            skLineSegment(sketch, "E174.2.0.7", {"start": v(-6.5, -37.5) * mm, "end": v(-3.5, -37.5) * mm});
            skLineSegment(sketch, "E174.2.0.8", {"start": v(-2, -42) * mm, "end": v(-2, -39.5) * mm});
            skLineSegment(sketch, "E174.2.0.9", {"start": v(-6.5, -39.5) * mm, "end": v(-6.5, -37.5) * mm});
            skLineSegment(sketch, "E174.2.0.10", {"start": v(-6.5, -46) * mm, "end": v(-6.5, -42) * mm});
            skLineSegment(sketch, "E174.2.0.11", {"start": v(-3.5, -39.5) * mm, "end": v(-2, -39.5) * mm});
            skLineSegment(sketch, "E174.2.0.12", {"start": v(-5, -46) * mm, "end": v(-5, -23) * mm, "construction": true});
            skLineSegment(sketch, "E174.direction1", {"start": v(353.5, -46) * mm, "end": v(313, -46) * mm, "construction": true});
            skLineSegment(sketch, "E175", {"start": v(318, -46) * mm, "end": v(313, -46) * mm});
            skLineSegment(sketch, "E176", {"start": v(187, -46) * mm, "end": v(176.5, -46) * mm});
            skLineSegment(sketch, "E177", {"start": v(173.5, -46) * mm, "end": v(163, -46) * mm});
            skLineSegment(sketch, "E178", {"start": v(143, -46) * mm, "end": v(138, -46) * mm});
            skLineSegment(sketch, "E179", {"start": v(12, -46) * mm, "end": v(-3.5, -46) * mm});
            skLineSegment(sketch, "E180", {"start": v(-6.5, -46) * mm, "end": v(-22, -46) * mm});
            skLineSegment(sketch, "E181.MirrorCS", {"start": v(172, -4) * mm, "end": v(173.5, -4) * mm});
            skLineSegment(sketch, "E182.MirrorCS", {"start": v(352, -6.5) * mm, "end": v(353.5, -6.5) * mm});
            skLineSegment(sketch, "E183.MirrorCS", {"start": v(-6.5, -6.5) * mm, "end": v(-6.5, -8.5) * mm});
            skLineSegment(sketch, "E184.MirrorCS", {"start": v(-8, -4) * mm, "end": v(-8, -6.5) * mm});
            skLineSegment(sketch, "E185.MirrorCS", {"start": v(-8, -4) * mm, "end": v(-6.5, -4) * mm});
            skLineSegment(sketch, "E186.MirrorCS", {"start": v(-3.5, -6.5) * mm, "end": v(-2, -6.5) * mm});
            skLineSegment(sketch, "E187.MirrorCS", {"start": v(173.5, 0) * mm, "end": v(173.5, -4) * mm});
            skLineSegment(sketch, "E188.MirrorCS", {"start": v(-2, -4) * mm, "end": v(-2, -6.5) * mm});
            skLineSegment(sketch, "E189.MirrorCS", {"start": v(-8, -6.5) * mm, "end": v(-6.5, -6.5) * mm});
            skLineSegment(sketch, "E190.MirrorCS", {"start": v(176.5, 0) * mm, "end": v(176.5, -4) * mm});
            skLineSegment(sketch, "E191.MirrorCS", {"start": v(172, -4) * mm, "end": v(172, -6.5) * mm});
            skLineSegment(sketch, "E192.MirrorCS", {"start": v(-6.5, -8.5) * mm, "end": v(-3.5, -8.5) * mm});
            skLineSegment(sketch, "E193.MirrorCS", {"start": v(-3.5, -4) * mm, "end": v(-2, -4) * mm});
            skLineSegment(sketch, "E194.MirrorCS", {"start": v(353.5, -8.5) * mm, "end": v(356.5, -8.5) * mm});
            skLineSegment(sketch, "E195.MirrorCS", {"start": v(353.5, -6.5) * mm, "end": v(353.5, -8.5) * mm});
            skLineSegment(sketch, "E196.MirrorCS", {"start": v(352, -4) * mm, "end": v(352, -6.5) * mm});
            skLineSegment(sketch, "E197.MirrorCS", {"start": v(176.5, -6.5) * mm, "end": v(176.5, -8.5) * mm});
            skLineSegment(sketch, "E198.MirrorCS", {"start": v(356.5, -6.5) * mm, "end": v(358, -6.5) * mm});
            skLineSegment(sketch, "E199.MirrorCS", {"start": v(-6.5, 0) * mm, "end": v(-6.5, -4) * mm});
            skLineSegment(sketch, "E200.MirrorCS", {"start": v(356.5, 0) * mm, "end": v(356.5, -4) * mm});
            skLineSegment(sketch, "E201.MirrorCS", {"start": v(353.5, 0) * mm, "end": v(353.5, -4) * mm});
            skLineSegment(sketch, "E202.MirrorCS", {"start": v(358, -4) * mm, "end": v(358, -6.5) * mm});
            skLineSegment(sketch, "E203.MirrorCS", {"start": v(176.5, -6.5) * mm, "end": v(178, -6.5) * mm});
            skLineSegment(sketch, "E204.MirrorCS", {"start": v(-3.5, -6.5) * mm, "end": v(-3.5, -8.5) * mm});
            skLineSegment(sketch, "E205.MirrorCS", {"start": v(356.5, -6.5) * mm, "end": v(356.5, -8.5) * mm});
            skLineSegment(sketch, "E206.MirrorCS", {"start": v(356.5, -4) * mm, "end": v(358, -4) * mm});
            skLineSegment(sketch, "E207.MirrorCS", {"start": v(172, -6.5) * mm, "end": v(173.5, -6.5) * mm});
            skLineSegment(sketch, "E208.MirrorCS", {"start": v(352, -4) * mm, "end": v(353.5, -4) * mm});
            skLineSegment(sketch, "E209.MirrorCS", {"start": v(176.5, -4) * mm, "end": v(178, -4) * mm});
            skLineSegment(sketch, "E210.MirrorCS", {"start": v(173.5, -8.5) * mm, "end": v(176.5, -8.5) * mm});
            skLineSegment(sketch, "E211.MirrorCS", {"start": v(178, -4) * mm, "end": v(178, -6.5) * mm});
            skLineSegment(sketch, "E212.MirrorCS", {"start": v(173.5, -6.5) * mm, "end": v(173.5, -8.5) * mm});
            skLineSegment(sketch, "E213.MirrorCS", {"start": v(143, 3) * mm, "end": v(143, 0) * mm});
            skLineSegment(sketch, "E214.MirrorCS", {"start": v(32, 0) * mm, "end": v(32, 3) * mm});
            skLineSegment(sketch, "E215.MirrorCS", {"start": v(187, 3) * mm, "end": v(187, 0) * mm});
            skLineSegment(sketch, "E216.MirrorCS", {"start": v(207, 0) * mm, "end": v(207, 3) * mm});
            skLineSegment(sketch, "E217.MirrorCS", {"start": v(187, 0) * mm, "end": v(176.5, 0) * mm});
            skLineSegment(sketch, "E218.MirrorCS", {"start": v(163, 0) * mm, "end": v(163, 3) * mm});
            skLineSegment(sketch, "E219.MirrorCS", {"start": v(338, 0) * mm, "end": v(338, 3) * mm});
            skLineSegment(sketch, "E220.MirrorCS", {"start": v(12, 3) * mm, "end": v(12, 0) * mm});
            skLineSegment(sketch, "E221.MirrorCS", {"start": v(328, 3) * mm, "end": v(328, 0) * mm, "construction": true});
            skLineSegment(sketch, "E222.MirrorCS", {"start": v(318, 3) * mm, "end": v(318, 0) * mm});
            skLineSegment(sketch, "E223.MirrorCS", {"start": v(173.5, 0) * mm, "end": v(163, 0) * mm});
            skLineSegment(sketch, "E224.MirrorCS", {"start": v(-3.5, 0) * mm, "end": v(-3.5, -4) * mm});
            skLineSegment(sketch, "E225.MirrorCS", {"start": v(353.5, 0) * mm, "end": v(338, 0) * mm});
            skLineSegment(sketch, "E226.MirrorCS", {"start": v(318, 0) * mm, "end": v(207, 0) * mm});
            skLineSegment(sketch, "E227.MirrorCS", {"start": v(153, 3) * mm, "end": v(153, 0) * mm, "construction": true});
            skLineSegment(sketch, "E228.MirrorCS", {"start": v(197, 3) * mm, "end": v(197, 0) * mm, "construction": true});
            skLineSegment(sketch, "E229.MirrorCS", {"start": v(22, 3) * mm, "end": v(22, 0) * mm, "construction": true});
            skLineSegment(sketch, "E230.MirrorCS", {"start": v(32, 3) * mm, "end": v(12, 3) * mm});
            skPoint(sketch, "E231.MirrorP", {"position": v(-5, -5.25) * mm});
            skLineSegment(sketch, "E232.MirrorCS", {"start": v(338, 3) * mm, "end": v(318, 3) * mm});
            skLineSegment(sketch, "E233.MirrorCS", {"start": v(372, -23) * mm, "end": v(372, 0) * mm});
            skLineSegment(sketch, "E234.MirrorCS", {"start": v(143, 0) * mm, "end": v(32, 0) * mm});
            skLineSegment(sketch, "E235.MirrorCS", {"start": v(355, 0) * mm, "end": v(355, -23) * mm, "construction": true});
            skPoint(sketch, "E236.MirrorP", {"position": v(355, -5.25) * mm});
            skLineSegment(sketch, "E237.MirrorCS", {"start": v(372, 0) * mm, "end": v(356.5, 0) * mm});
            skLineSegment(sketch, "E238.MirrorCS", {"start": v(-5, 0) * mm, "end": v(-5, -23) * mm, "construction": true});
            skLineSegment(sketch, "E239.MirrorCS", {"start": v(12, 0) * mm, "end": v(-3.5, 0) * mm});
            skPoint(sketch, "E240.MirrorP", {"position": v(372, 0) * mm});
            skLineSegment(sketch, "E241.MirrorCS", {"start": v(-22, -23) * mm, "end": v(-22, 0) * mm});
            skLineSegment(sketch, "E242.MirrorCS", {"start": v(-6.5, 0) * mm, "end": v(-22, 0) * mm});
            skPoint(sketch, "E243.MirrorP", {"position": v(-22, 0) * mm});
            skLineSegment(sketch, "E244.MirrorCS", {"start": v(353.5, 0) * mm, "end": v(173.5, 0) * mm, "construction": true});
            skPoint(sketch, "E245.MirrorP", {"position": v(175, -5.25) * mm});
            skLineSegment(sketch, "E246.MirrorCS", {"start": v(207, 3) * mm, "end": v(187, 3) * mm});
            skLineSegment(sketch, "E247.MirrorCS", {"start": v(163, 3) * mm, "end": v(143, 3) * mm});
            skLineSegment(sketch, "E248.MirrorCS", {"start": v(175, 0) * mm, "end": v(175, -23) * mm, "construction": true});
            skLineSegment(sketch, "E249", {"start": v(138, -46) * mm, "end": v(138, -44.5) * mm});
            skLineSegment(sketch, "E250", {"start": v(136.5, -43) * mm, "end": v(131.5, -43) * mm});
            skLineSegment(sketch, "E251", {"start": v(130, -44.5) * mm, "end": v(130, -46) * mm});
            skLineSegment(sketch, "E252.trimOffspring", {"start": v(130, -46) * mm, "end": v(102.5, -46) * mm});
            skPoint(sketch, "E253.visualSharp", {"position": v(130, -43) * mm});
            skArc(sketch, "E253.filletArc", {"start": v(131.5, -43) * mm, "mid": v(130.44, -43.44) * mm, "end": v(130, -44.5) * mm});
            skPoint(sketch, "E254.visualSharp", {"position": v(138, -43) * mm});
            skArc(sketch, "E254.filletArc", {"start": v(138, -44.5) * mm, "mid": v(137.56, -43.44) * mm, "end": v(136.5, -43) * mm});
            skLineSegment(sketch, "E255", {"start": v(37, -46) * mm, "end": v(37, -44.5) * mm});
            skLineSegment(sketch, "E256", {"start": v(38.5, -43) * mm, "end": v(43.5, -43) * mm});
            skLineSegment(sketch, "E257", {"start": v(45, -44.5) * mm, "end": v(45, -46) * mm});
            skLineSegment(sketch, "E258.trimOffspring", {"start": v(37, -46) * mm, "end": v(32, -46) * mm});
            skPoint(sketch, "E259.visualSharp", {"position": v(45, -43) * mm});
            skArc(sketch, "E259.filletArc", {"start": v(45, -44.5) * mm, "mid": v(44.56, -43.44) * mm, "end": v(43.5, -43) * mm});
            skPoint(sketch, "E260.visualSharp", {"position": v(37, -43) * mm});
            skArc(sketch, "E260.filletArc", {"start": v(38.5, -43) * mm, "mid": v(37.44, -43.44) * mm, "end": v(37, -44.5) * mm});
            skLineSegment(sketch, "E261", {"start": v(313, -46) * mm, "end": v(313, -44.5) * mm});
            skLineSegment(sketch, "E262", {"start": v(311.5, -43) * mm, "end": v(306.5, -43) * mm});
            skLineSegment(sketch, "E263", {"start": v(305, -44.5) * mm, "end": v(305, -46) * mm});
            skPoint(sketch, "E264.visualSharp", {"position": v(305, -43) * mm});
            skArc(sketch, "E264.filletArc", {"start": v(306.5, -43) * mm, "mid": v(305.44, -43.44) * mm, "end": v(305, -44.5) * mm});
            skPoint(sketch, "E265.visualSharp", {"position": v(313, -43) * mm});
            skArc(sketch, "E265.filletArc", {"start": v(313, -44.5) * mm, "mid": v(312.56, -43.44) * mm, "end": v(311.5, -43) * mm});
            skLineSegment(sketch, "E266.trimOffspring", {"start": v(305, -46) * mm, "end": v(173.5, -46) * mm, "construction": true});
            skLineSegment(sketch, "E267.trimOffspring", {"start": v(305, -46) * mm, "end": v(207, -46) * mm});
            skLineSegment(sketch, "E268", {"start": v(87.5, -46) * mm, "end": v(87.5, -23) * mm, "construction": true});
            skLineSegment(sketch, "E269", {"start": v(102.5, -46) * mm, "end": v(102.5, -44.5) * mm});
            skLineSegment(sketch, "E270", {"start": v(101, -43) * mm, "end": v(74, -43) * mm});
            skLineSegment(sketch, "E271", {"start": v(72.5, -44.5) * mm, "end": v(72.5, -46) * mm});
            skPoint(sketch, "E272", {"position": v(87.5, -43) * mm});
            skLineSegment(sketch, "E273.trimOffspring", {"start": v(72.5, -46) * mm, "end": v(45, -46) * mm});
            skPoint(sketch, "E274.visualSharp", {"position": v(102.5, -43) * mm});
            skArc(sketch, "E274.filletArc", {"start": v(102.5, -44.5) * mm, "mid": v(102.06, -43.44) * mm, "end": v(101, -43) * mm});
            skPoint(sketch, "E275.visualSharp", {"position": v(72.5, -43) * mm});
            skArc(sketch, "E275.filletArc", {"start": v(74, -43) * mm, "mid": v(72.94, -43.44) * mm, "end": v(72.5, -44.5) * mm});
            skSolve(sketch);
        }
        {
            var Q0;
            Q0=makeQuery(id+"F10.imprint","IMPRINT",FACE,{"disambiguationData":[TD([[makeQuery(id+"F10.imprint","IMPRINT",EDGE,{"derivedFrom":sQuery(id+"F10.wireOp",EDGE,"E147")}),-1.0]])]});
            extrude(context, id + "F11", {"entities" : qUnion([Q0]), "depth" : 6 * mm, "symmetric" : true});
        }
        {
            var Q0;
            Q0=makeQuery(id+"F11.opExtrude","SWEPT_BODY",BODY,{"disambiguationData":[OSD([sQuery(id+"F10.wireOp",EDGE,"E147"),sQuery(id+"F10.wireOp",EDGE,"E148"),sQuery(id+"F10.wireOp",EDGE,"KtgLcZro-Gi18-2paL-ronS-uR46lsXsDt71.bottom"),sQuery(id+"F10.wireOp",EDGE,"KtgLcZro-Gi18-2paL-ronS-uR46lsXsDt71.left"),sQuery(id+"F10.wireOp",EDGE,"KtgLcZro-Gi18-2paL-ronS-uR46lsXsDt71.right"),sQuery(id+"F10.wireOp",EDGE,"GIBqVv8B-Go3L-kjrv-fow0-1hPMpe5xOsCY.bottom"),sQuery(id+"F10.wireOp",EDGE,"GIBqVv8B-Go3L-kjrv-fow0-1hPMpe5xOsCY.left"),sQuery(id+"F10.wireOp",EDGE,"GIBqVv8B-Go3L-kjrv-fow0-1hPMpe5xOsCY.right"),sQuery(id+"F10.wireOp",EDGE,"C6l01rvX-xXIv-Yw3v-4MLj-VURo6Fi3yfat"),sQuery(id+"F10.wireOp",EDGE,"SJWZGjJp-2Uf8-EYLt-dNml-pFZFEXsSqGbw.bottom"),sQuery(id+"F10.wireOp",EDGE,"SJWZGjJp-2Uf8-EYLt-dNml-pFZFEXsSqGbw.left"),sQuery(id+"F10.wireOp",EDGE,"SJWZGjJp-2Uf8-EYLt-dNml-pFZFEXsSqGbw.right"),sQuery(id+"F10.wireOp",EDGE,"0VWDFySL-sPqn-z3Gb-qFFI-h3bUQO7hZhO1.bottom"),sQuery(id+"F10.wireOp",EDGE,"0VWDFySL-sPqn-z3Gb-qFFI-h3bUQO7hZhO1.left"),sQuery(id+"F10.wireOp",EDGE,"0VWDFySL-sPqn-z3Gb-qFFI-h3bUQO7hZhO1.right"),sQuery(id+"F10.wireOp",EDGE,"E150.top"),sQuery(id+"F10.wireOp",EDGE,"E150.left"),sQuery(id+"F10.wireOp",EDGE,"E150.right"),sQuery(id+"F10.wireOp",EDGE,"E151.bottom"),sQuery(id+"F10.wireOp",EDGE,"E151.top"),sQuery(id+"F10.wireOp",EDGE,"E151.left"),sQuery(id+"F10.wireOp",EDGE,"E151.right"),sQuery(id+"F10.wireOp",EDGE,"E152.trimOffspring"),sQuery(id+"F10.wireOp",EDGE,"E153.trimOffspring"),sQuery(id+"F10.wireOp",EDGE,"E154.trimOffspring"),sQuery(id+"F10.wireOp",EDGE,"E155.trimOffspring"),sQuery(id+"F10.wireOp",EDGE,"e2a2db74-9ea7-42a8-bf58-83d2eb57d682.trimOffspring"),sQuery(id+"F10.wireOp",EDGE,"34e65598-81c8-4b1d-b155-a18f7778bf65.1.0.0"),sQuery(id+"F10.wireOp",EDGE,"34e65598-81c8-4b1d-b155-a18f7778bf65.1.0.1"),sQuery(id+"F10.wireOp",EDGE,"34e65598-81c8-4b1d-b155-a18f7778bf65.1.0.2"),sQuery(id+"F10.wireOp",EDGE,"34e65598-81c8-4b1d-b155-a18f7778bf65.1.0.3"),sQuery(id+"F10.wireOp",EDGE,"34e65598-81c8-4b1d-b155-a18f7778bf65.1.0.4"),sQuery(id+"F10.wireOp",EDGE,"34e65598-81c8-4b1d-b155-a18f7778bf65.1.0.5"),sQuery(id+"F10.wireOp",EDGE,"34e65598-81c8-4b1d-b155-a18f7778bf65.1.0.6"),sQuery(id+"F10.wireOp",EDGE,"34e65598-81c8-4b1d-b155-a18f7778bf65.1.0.9"),sQuery(id+"F10.wireOp",EDGE,"34e65598-81c8-4b1d-b155-a18f7778bf65.1.0.10"),sQuery(id+"F10.wireOp",EDGE,"34e65598-81c8-4b1d-b155-a18f7778bf65.1.0.11"),sQuery(id+"F10.wireOp",EDGE,"34e65598-81c8-4b1d-b155-a18f7778bf65.1.0.12"),sQuery(id+"F10.wireOp",EDGE,"34e65598-81c8-4b1d-b155-a18f7778bf65.2.0.0"),sQuery(id+"F10.wireOp",EDGE,"34e65598-81c8-4b1d-b155-a18f7778bf65.2.0.1"),sQuery(id+"F10.wireOp",EDGE,"34e65598-81c8-4b1d-b155-a18f7778bf65.2.0.2"),sQuery(id+"F10.wireOp",EDGE,"34e65598-81c8-4b1d-b155-a18f7778bf65.2.0.3"),sQuery(id+"F10.wireOp",EDGE,"34e65598-81c8-4b1d-b155-a18f7778bf65.2.0.4"),sQuery(id+"F10.wireOp",EDGE,"34e65598-81c8-4b1d-b155-a18f7778bf65.2.0.5"),sQuery(id+"F10.wireOp",EDGE,"34e65598-81c8-4b1d-b155-a18f7778bf65.2.0.6"),sQuery(id+"F10.wireOp",EDGE,"34e65598-81c8-4b1d-b155-a18f7778bf65.2.0.9"),sQuery(id+"F10.wireOp",EDGE,"34e65598-81c8-4b1d-b155-a18f7778bf65.2.0.10"),sQuery(id+"F10.wireOp",EDGE,"34e65598-81c8-4b1d-b155-a18f7778bf65.2.0.11"),sQuery(id+"F10.wireOp",EDGE,"34e65598-81c8-4b1d-b155-a18f7778bf65.2.0.12"),sQuery(id+"F10.wireOp",EDGE,"34e65598-81c8-4b1d-b155-a18f7778bf65.3.0.0"),sQuery(id+"F10.wireOp",EDGE,"34e65598-81c8-4b1d-b155-a18f7778bf65.3.0.1"),sQuery(id+"F10.wireOp",EDGE,"34e65598-81c8-4b1d-b155-a18f7778bf65.3.0.2"),sQuery(id+"F10.wireOp",EDGE,"34e65598-81c8-4b1d-b155-a18f7778bf65.3.0.3"),sQuery(id+"F10.wireOp",EDGE,"34e65598-81c8-4b1d-b155-a18f7778bf65.3.0.4"),sQuery(id+"F10.wireOp",EDGE,"34e65598-81c8-4b1d-b155-a18f7778bf65.3.0.5"),sQuery(id+"F10.wireOp",EDGE,"34e65598-81c8-4b1d-b155-a18f7778bf65.3.0.6"),sQuery(id+"F10.wireOp",EDGE,"34e65598-81c8-4b1d-b155-a18f7778bf65.3.0.9"),sQuery(id+"F10.wireOp",EDGE,"34e65598-81c8-4b1d-b155-a18f7778bf65.3.0.10"),sQuery(id+"F10.wireOp",EDGE,"34e65598-81c8-4b1d-b155-a18f7778bf65.3.0.11"),sQuery(id+"F10.wireOp",EDGE,"34e65598-81c8-4b1d-b155-a18f7778bf65.3.0.12"),sQuery(id+"F10.wireOp",EDGE,"34e65598-81c8-4b1d-b155-a18f7778bf65.4.0.0"),sQuery(id+"F10.wireOp",EDGE,"34e65598-81c8-4b1d-b155-a18f7778bf65.4.0.1"),sQuery(id+"F10.wireOp",EDGE,"34e65598-81c8-4b1d-b155-a18f7778bf65.4.0.2"),sQuery(id+"F10.wireOp",EDGE,"34e65598-81c8-4b1d-b155-a18f7778bf65.4.0.3"),sQuery(id+"F10.wireOp",EDGE,"34e65598-81c8-4b1d-b155-a18f7778bf65.4.0.4"),sQuery(id+"F10.wireOp",EDGE,"34e65598-81c8-4b1d-b155-a18f7778bf65.4.0.5"),sQuery(id+"F10.wireOp",EDGE,"34e65598-81c8-4b1d-b155-a18f7778bf65.4.0.6"),sQuery(id+"F10.wireOp",EDGE,"34e65598-81c8-4b1d-b155-a18f7778bf65.4.0.9"),sQuery(id+"F10.wireOp",EDGE,"34e65598-81c8-4b1d-b155-a18f7778bf65.4.0.10"),sQuery(id+"F10.wireOp",EDGE,"34e65598-81c8-4b1d-b155-a18f7778bf65.4.0.11"),sQuery(id+"F10.wireOp",EDGE,"34e65598-81c8-4b1d-b155-a18f7778bf65.4.0.12"),sQuery(id+"F10.wireOp",EDGE,"AtrAxSzi-Mmhj-RrMe-m420-yhNJprFXGALF"),sQuery(id+"F10.wireOp",EDGE,"lsJKj0vL-nqnl-Pig2-pSDZ-BF5X5dBvlvuk"),sQuery(id+"F10.wireOp",EDGE,"mF3yHTbz-levo-uQwc-hIwJ-Var4NT9WmbZd"),sQuery(id+"F10.wireOp",EDGE,"RwohxFWo-UmZY-efgO-1pcA-N4gNC5kNnMMc"),sQuery(id+"F10.wireOp",EDGE,"uLZdnxeG-Dstg-KTGM-59cl-1tGhg9vy4fDV"),sQuery(id+"F10.wireOp",EDGE,"H1VDkdzY-lGSu-WIwh-F6iC-p8I3ZvxELqng"),sQuery(id+"F10.wireOp",EDGE,"9gcYdVeQ-W2WW-HFgy-HcfS-cgZgbH94FxqF"),sQuery(id+"F10.wireOp",EDGE,"xgz2xgPr-RkPn-GdoT-1YOE-1HAzlw55qboS"),sQuery(id+"F10.wireOp",EDGE,"b53dad86-37d2-494f-a81a-d3a14931b3960.MirrorCS"),sQuery(id+"F10.wireOp",EDGE,"b53dad86-37d2-494f-a81a-d3a14931b3961.MirrorCS"),sQuery(id+"F10.wireOp",EDGE,"b53dad86-37d2-494f-a81a-d3a14931b3962.MirrorCS"),sQuery(id+"F10.wireOp",EDGE,"b53dad86-37d2-494f-a81a-d3a14931b3963.MirrorCS"),sQuery(id+"F10.wireOp",EDGE,"b53dad86-37d2-494f-a81a-d3a14931b3964.MirrorCS"),sQuery(id+"F10.wireOp",EDGE,"b53dad86-37d2-494f-a81a-d3a14931b3965.MirrorCS"),sQuery(id+"F10.wireOp",EDGE,"b53dad86-37d2-494f-a81a-d3a14931b3966.MirrorCS"),sQuery(id+"F10.wireOp",EDGE,"b53dad86-37d2-494f-a81a-d3a14931b3967.MirrorCS"),sQuery(id+"F10.wireOp",EDGE,"b53dad86-37d2-494f-a81a-d3a14931b3968.MirrorCS"),sQuery(id+"F10.wireOp",EDGE,"b53dad86-37d2-494f-a81a-d3a14931b3969.MirrorCS"),sQuery(id+"F10.wireOp",EDGE,"b53dad86-37d2-494f-a81a-d3a14931b39610.MirrorCS"),sQuery(id+"F10.wireOp",EDGE,"b53dad86-37d2-494f-a81a-d3a14931b39611.MirrorCS"),sQuery(id+"F10.wireOp",EDGE,"b53dad86-37d2-494f-a81a-d3a14931b39612.MirrorCS"),sQuery(id+"F10.wireOp",EDGE,"b53dad86-37d2-494f-a81a-d3a14931b39613.MirrorCS"),sQuery(id+"F10.wireOp",EDGE,"b53dad86-37d2-494f-a81a-d3a14931b39614.MirrorCS"),sQuery(id+"F10.wireOp",EDGE,"b53dad86-37d2-494f-a81a-d3a14931b39615.MirrorCS"),sQuery(id+"F10.wireOp",EDGE,"b53dad86-37d2-494f-a81a-d3a14931b39616.MirrorCS"),sQuery(id+"F10.wireOp",EDGE,"b53dad86-37d2-494f-a81a-d3a14931b39617.MirrorCS"),sQuery(id+"F10.wireOp",EDGE,"b53dad86-37d2-494f-a81a-d3a14931b39618.MirrorCS"),sQuery(id+"F10.wireOp",EDGE,"b53dad86-37d2-494f-a81a-d3a14931b39619.MirrorCS"),sQuery(id+"F10.wireOp",EDGE,"b53dad86-37d2-494f-a81a-d3a14931b39620.MirrorCS"),sQuery(id+"F10.wireOp",EDGE,"b53dad86-37d2-494f-a81a-d3a14931b39621.MirrorCS"),sQuery(id+"F10.wireOp",EDGE,"b53dad86-37d2-494f-a81a-d3a14931b39622.MirrorCS"),sQuery(id+"F10.wireOp",EDGE,"b53dad86-37d2-494f-a81a-d3a14931b39623.MirrorCS"),sQuery(id+"F10.wireOp",EDGE,"b53dad86-37d2-494f-a81a-d3a14931b39624.MirrorCS"),sQuery(id+"F10.wireOp",EDGE,"b53dad86-37d2-494f-a81a-d3a14931b39625.MirrorCS"),sQuery(id+"F10.wireOp",EDGE,"b53dad86-37d2-494f-a81a-d3a14931b39626.MirrorCS"),sQuery(id+"F10.wireOp",EDGE,"b53dad86-37d2-494f-a81a-d3a14931b39627.MirrorCS"),sQuery(id+"F10.wireOp",EDGE,"b53dad86-37d2-494f-a81a-d3a14931b39628.MirrorCS"),sQuery(id+"F10.wireOp",EDGE,"b53dad86-37d2-494f-a81a-d3a14931b39629.MirrorCS"),sQuery(id+"F10.wireOp",EDGE,"b53dad86-37d2-494f-a81a-d3a14931b39630.MirrorCS"),sQuery(id+"F10.wireOp",EDGE,"b53dad86-37d2-494f-a81a-d3a14931b39631.MirrorCS"),sQuery(id+"F10.wireOp",EDGE,"b53dad86-37d2-494f-a81a-d3a14931b39632.MirrorCS"),sQuery(id+"F10.wireOp",EDGE,"b53dad86-37d2-494f-a81a-d3a14931b39633.MirrorCS"),sQuery(id+"F10.wireOp",EDGE,"b53dad86-37d2-494f-a81a-d3a14931b39634.MirrorCS"),sQuery(id+"F10.wireOp",EDGE,"b53dad86-37d2-494f-a81a-d3a14931b39635.MirrorCS"),sQuery(id+"F10.wireOp",EDGE,"b53dad86-37d2-494f-a81a-d3a14931b39636.MirrorCS"),sQuery(id+"F10.wireOp",EDGE,"b53dad86-37d2-494f-a81a-d3a14931b39637.MirrorCS"),sQuery(id+"F10.wireOp",EDGE,"b53dad86-37d2-494f-a81a-d3a14931b39638.MirrorCS"),sQuery(id+"F10.wireOp",EDGE,"b53dad86-37d2-494f-a81a-d3a14931b39639.MirrorCS"),sQuery(id+"F10.wireOp",EDGE,"b53dad86-37d2-494f-a81a-d3a14931b39640.MirrorCS"),sQuery(id+"F10.wireOp",EDGE,"b53dad86-37d2-494f-a81a-d3a14931b39641.MirrorCS"),sQuery(id+"F10.wireOp",EDGE,"b53dad86-37d2-494f-a81a-d3a14931b39642.MirrorCS"),sQuery(id+"F10.wireOp",EDGE,"b53dad86-37d2-494f-a81a-d3a14931b39643.MirrorCS"),sQuery(id+"F10.wireOp",EDGE,"b53dad86-37d2-494f-a81a-d3a14931b39644.MirrorCS"),sQuery(id+"F10.wireOp",EDGE,"b53dad86-37d2-494f-a81a-d3a14931b39645.MirrorCS"),sQuery(id+"F10.wireOp",EDGE,"b53dad86-37d2-494f-a81a-d3a14931b39647.MirrorCS"),sQuery(id+"F10.wireOp",EDGE,"b53dad86-37d2-494f-a81a-d3a14931b39648.MirrorCS"),sQuery(id+"F10.wireOp",EDGE,"b53dad86-37d2-494f-a81a-d3a14931b39649.MirrorCS"),sQuery(id+"F10.wireOp",EDGE,"b53dad86-37d2-494f-a81a-d3a14931b39650.MirrorCS"),sQuery(id+"F10.wireOp",EDGE,"b53dad86-37d2-494f-a81a-d3a14931b39651.MirrorCS"),sQuery(id+"F10.wireOp",EDGE,"b53dad86-37d2-494f-a81a-d3a14931b39652.MirrorCS"),sQuery(id+"F10.wireOp",EDGE,"b53dad86-37d2-494f-a81a-d3a14931b39653.MirrorCS"),sQuery(id+"F10.wireOp",EDGE,"b53dad86-37d2-494f-a81a-d3a14931b39654.MirrorCS"),sQuery(id+"F10.wireOp",EDGE,"b53dad86-37d2-494f-a81a-d3a14931b39655.MirrorCS"),sQuery(id+"F10.wireOp",EDGE,"b53dad86-37d2-494f-a81a-d3a14931b39656.MirrorCS"),sQuery(id+"F10.wireOp",EDGE,"b53dad86-37d2-494f-a81a-d3a14931b39657.MirrorCS"),sQuery(id+"F10.wireOp",EDGE,"b53dad86-37d2-494f-a81a-d3a14931b39658.MirrorCS"),sQuery(id+"F10.wireOp",EDGE,"b53dad86-37d2-494f-a81a-d3a14931b39659.MirrorCS"),sQuery(id+"F10.wireOp",EDGE,"b53dad86-37d2-494f-a81a-d3a14931b39660.MirrorCS"),sQuery(id+"F10.wireOp",EDGE,"b53dad86-37d2-494f-a81a-d3a14931b39661.MirrorCS"),sQuery(id+"F10.wireOp",EDGE,"b53dad86-37d2-494f-a81a-d3a14931b39662.MirrorCS"),sQuery(id+"F10.wireOp",EDGE,"b53dad86-37d2-494f-a81a-d3a14931b39664.MirrorCS"),sQuery(id+"F10.wireOp",EDGE,"b53dad86-37d2-494f-a81a-d3a14931b39667.MirrorCS"),sQuery(id+"F10.wireOp",EDGE,"b53dad86-37d2-494f-a81a-d3a14931b39670.MirrorCS"),sQuery(id+"F10.wireOp",EDGE,"b53dad86-37d2-494f-a81a-d3a14931b39676.MirrorCS"),sQuery(id+"F10.wireOp",EDGE,"b53dad86-37d2-494f-a81a-d3a14931b39679.MirrorCS"),sQuery(id+"F10.wireOp",EDGE,"b53dad86-37d2-494f-a81a-d3a14931b39680.MirrorCS"),sQuery(id+"F10.wireOp",EDGE,"b53dad86-37d2-494f-a81a-d3a14931b39682.MirrorCS"),sQuery(id+"F10.wireOp",EDGE,"b53dad86-37d2-494f-a81a-d3a14931b39683.MirrorCS"),sQuery(id+"F10.wireOp",EDGE,"b53dad86-37d2-494f-a81a-d3a14931b39685.MirrorCS"),sQuery(id+"F10.wireOp",EDGE,"b53dad86-37d2-494f-a81a-d3a14931b39689.MirrorCS"),sQuery(id+"F10.wireOp",EDGE,"b53dad86-37d2-494f-a81a-d3a14931b39691.MirrorCS"),sQuery(id+"F10.wireOp",EDGE,"b53dad86-37d2-494f-a81a-d3a14931b39692.MirrorCS"),sQuery(id+"F10.wireOp",EDGE,"b53dad86-37d2-494f-a81a-d3a14931b39698.MirrorCS"),sQuery(id+"F10.wireOp",EDGE,"b53dad86-37d2-494f-a81a-d3a14931b396102.MirrorCS"),sQuery(id+"F10.wireOp",EDGE,"b53dad86-37d2-494f-a81a-d3a14931b396104.MirrorCS"),sQuery(id+"F10.wireOp",EDGE,"b53dad86-37d2-494f-a81a-d3a14931b396105.MirrorCS"),sQuery(id+"F10.wireOp",EDGE,"b53dad86-37d2-494f-a81a-d3a14931b396106.MirrorCS")])]});
            var Q1;
            Q1=makeQuery(id+"F6.opExtrude","SWEPT_BODY",BODY,{"disambiguationData":[OSD([sQuery(id+"F5.wireOp",EDGE,"E96.0"),sQuery(id+"F5.wireOp",EDGE,"E97.0"),sQuery(id+"F5.wireOp",EDGE,"E98.0"),sQuery(id+"F5.wireOp",EDGE,"E99.0"),sQuery(id+"F5.wireOp",EDGE,"E100.0"),sQuery(id+"F5.wireOp",EDGE,"E101.0"),sQuery(id+"F5.wireOp",EDGE,"E102.0"),sQuery(id+"F5.wireOp",EDGE,"E103.0"),sQuery(id+"F5.wireOp",EDGE,"E104.0"),sQuery(id+"F5.wireOp",EDGE,"E105.0"),sQuery(id+"F5.wireOp",EDGE,"E106"),sQuery(id+"F5.wireOp",EDGE,"E107.1.0.0"),sQuery(id+"F5.wireOp",EDGE,"E107.2.0.0"),sQuery(id+"F5.wireOp",EDGE,"E109.0"),sQuery(id+"F5.wireOp",EDGE,"E110.0"),sQuery(id+"F5.wireOp",EDGE,"E111.0"),sQuery(id+"F5.wireOp",EDGE,"E112.0"),sQuery(id+"F5.wireOp",EDGE,"E112.1"),sQuery(id+"F5.wireOp",EDGE,"E112.2"),sQuery(id+"F5.wireOp",EDGE,"E112.3"),sQuery(id+"F5.wireOp",EDGE,"E113.MirrorC"),sQuery(id+"F5.wireOp",EDGE,"E114.MirrorC"),sQuery(id+"F5.wireOp",EDGE,"E115.MirrorC"),sQuery(id+"F5.wireOp",EDGE,"E116.MirrorC"),sQuery(id+"F5.wireOp",EDGE,"E117.MirrorC"),sQuery(id+"F5.wireOp",EDGE,"E118.MirrorC"),sQuery(id+"F5.wireOp",EDGE,"E119.MirrorC"),sQuery(id+"F5.wireOp",EDGE,"E120.MirrorCS"),sQuery(id+"F5.wireOp",EDGE,"E122.MirrorCS"),sQuery(id+"F5.wireOp",EDGE,"E123.MirrorCS"),sQuery(id+"F5.wireOp",EDGE,"E124.MirrorCS"),sQuery(id+"F5.wireOp",EDGE,"E125.MirrorCS"),sQuery(id+"F5.wireOp",EDGE,"E126.MirrorCS"),sQuery(id+"F5.wireOp",EDGE,"E127.MirrorCS"),sQuery(id+"F5.wireOp",EDGE,"E128.MirrorCS"),sQuery(id+"F5.wireOp",EDGE,"E129.MirrorCS"),sQuery(id+"F5.wireOp",EDGE,"E130.MirrorCS"),sQuery(id+"F5.wireOp",EDGE,"E132.MirrorCS")])]});
            var Q2;
            Q2=makeQuery(id+"F3.opExtrude","SWEPT_BODY",BODY,{"disambiguationData":[OSD([sQuery(id+"F0T68XCoUrNjqKc_0.merge.FRI3efolS22JnH9_0.merge.F2le2PEO98lg6xs_0.merge.FXX2dDxdAnKxtOb_1.wireOp",EDGE,"a45bbf6a-1b3a-4c73-aa77-97d7b8075cbb"),sQuery(id+"F2.wireOp",EDGE,"E0"),sQuery(id+"F2.wireOp",EDGE,"E1"),sQuery(id+"F2.wireOp",EDGE,"E3.MirrorCS"),sQuery(id+"F2.wireOp",EDGE,"E4"),sQuery(id+"F2.wireOp",EDGE,"E5.1.0.0"),sQuery(id+"F2.wireOp",EDGE,"E5.1.0.1"),sQuery(id+"F2.wireOp",EDGE,"E5.1.0.2"),sQuery(id+"F2.wireOp",EDGE,"E5.2.0.0"),sQuery(id+"F2.wireOp",EDGE,"E5.2.0.2"),sQuery(id+"F2.wireOp",EDGE,"E6"),sQuery(id+"F2.wireOp",EDGE,"E9"),sQuery(id+"F2.wireOp",EDGE,"E10.1.0.0"),sQuery(id+"F2.wireOp",EDGE,"E10.1.0.1"),sQuery(id+"F2.wireOp",EDGE,"E5.2.0.1"),sQuery(id+"F2.wireOp",EDGE,"E10.2.0.0"),sQuery(id+"F2.wireOp",EDGE,"E10.2.0.1"),sQuery(id+"F2.wireOp",EDGE,"E13"),sQuery(id+"F2.wireOp",EDGE,"E14"),sQuery(id+"F2.wireOp",EDGE,"E15"),sQuery(id+"F2.wireOp",EDGE,"E16"),sQuery(id+"F2.wireOp",EDGE,"E18.MirrorC"),sQuery(id+"F2.wireOp",EDGE,"E17.MirrorC"),sQuery(id+"F2.wireOp",EDGE,"E20.rect.bottom"),sQuery(id+"F2.wireOp",EDGE,"E20.rect.top"),sQuery(id+"F2.wireOp",EDGE,"E20.rect.left"),sQuery(id+"F2.wireOp",EDGE,"E20.rect.right"),sQuery(id+"F2.wireOp",EDGE,"E21.filletArc"),sQuery(id+"F2.wireOp",EDGE,"E22.filletArc"),sQuery(id+"F2.wireOp",EDGE,"E23.filletArc"),sQuery(id+"F2.wireOp",EDGE,"E24.filletArc"),sQuery(id+"F2.wireOp",EDGE,"E25.1.0.0"),sQuery(id+"F2.wireOp",EDGE,"E25.1.0.3"),sQuery(id+"F2.wireOp",EDGE,"E25.1.0.5"),sQuery(id+"F2.wireOp",EDGE,"E25.1.0.8"),sQuery(id+"F2.wireOp",EDGE,"E25.1.0.9"),sQuery(id+"F2.wireOp",EDGE,"E25.1.0.10"),sQuery(id+"F2.wireOp",EDGE,"E25.1.0.11"),sQuery(id+"F2.wireOp",EDGE,"E25.1.0.12"),sQuery(id+"F2.wireOp",EDGE,"E25.2.0.0"),sQuery(id+"F2.wireOp",EDGE,"E25.2.0.3"),sQuery(id+"F2.wireOp",EDGE,"E25.2.0.5"),sQuery(id+"F2.wireOp",EDGE,"E25.2.0.8"),sQuery(id+"F2.wireOp",EDGE,"E25.2.0.9"),sQuery(id+"F2.wireOp",EDGE,"E25.2.0.10"),sQuery(id+"F2.wireOp",EDGE,"E25.2.0.11"),sQuery(id+"F2.wireOp",EDGE,"E25.2.0.12"),sQuery(id+"F2.wireOp",EDGE,"E26.MirrorCS"),sQuery(id+"F2.wireOp",EDGE,"E27.MirrorCS"),sQuery(id+"F2.wireOp",EDGE,"E28.MirrorCS"),sQuery(id+"F2.wireOp",EDGE,"E29.MirrorCS"),sQuery(id+"F2.wireOp",EDGE,"E30.MirrorCS"),sQuery(id+"F2.wireOp",EDGE,"E31.MirrorCS"),sQuery(id+"F2.wireOp",EDGE,"E32.MirrorCS"),sQuery(id+"F2.wireOp",EDGE,"E33.MirrorCS"),sQuery(id+"F2.wireOp",EDGE,"E34.MirrorCS"),sQuery(id+"F2.wireOp",EDGE,"E35.MirrorCS"),sQuery(id+"F2.wireOp",EDGE,"E36.MirrorCS"),sQuery(id+"F2.wireOp",EDGE,"E37.MirrorCS"),sQuery(id+"F2.wireOp",EDGE,"E38.MirrorCS"),sQuery(id+"F2.wireOp",EDGE,"E39.MirrorCS"),sQuery(id+"F2.wireOp",EDGE,"E40.MirrorCS"),sQuery(id+"F2.wireOp",EDGE,"E41.MirrorCS"),sQuery(id+"F2.wireOp",EDGE,"E42.MirrorCS"),sQuery(id+"F2.wireOp",EDGE,"E43.MirrorCS"),sQuery(id+"F2.wireOp",EDGE,"E44.MirrorCS"),sQuery(id+"F2.wireOp",EDGE,"E45.MirrorCS"),sQuery(id+"F2.wireOp",EDGE,"E46.MirrorCS"),sQuery(id+"F2.wireOp",EDGE,"E47.MirrorCS"),sQuery(id+"F2.wireOp",EDGE,"E48.MirrorCS"),sQuery(id+"F2.wireOp",EDGE,"E49.MirrorC"),sQuery(id+"F2.wireOp",EDGE,"E50.MirrorC"),sQuery(id+"F2.wireOp",EDGE,"E51.MirrorC"),sQuery(id+"F2.wireOp",EDGE,"E52.MirrorC"),sQuery(id+"F2.wireOp",EDGE,"E54.MirrorC"),sQuery(id+"F2.wireOp",EDGE,"E55.MirrorC"),sQuery(id+"F2.wireOp",EDGE,"E57.MirrorC"),sQuery(id+"F2.wireOp",EDGE,"E64.MirrorCS"),sQuery(id+"F2.wireOp",EDGE,"E65.MirrorCS"),sQuery(id+"F2.wireOp",EDGE,"E67.MirrorCS"),sQuery(id+"F2.wireOp",EDGE,"E68.MirrorC"),sQuery(id+"F2.wireOp",EDGE,"E71.MirrorCS"),sQuery(id+"F2.wireOp",EDGE,"E73.MirrorC"),sQuery(id+"F2.wireOp",EDGE,"E75.MirrorCS"),sQuery(id+"F2.wireOp",EDGE,"E76.MirrorCS"),sQuery(id+"F2.wireOp",EDGE,"E79.MirrorCS"),sQuery(id+"F2.wireOp",EDGE,"E81.MirrorCS"),sQuery(id+"F2.wireOp",EDGE,"E83.MirrorCS"),sQuery(id+"F2.wireOp",EDGE,"E84.MirrorCS"),sQuery(id+"F2.wireOp",EDGE,"E53.MirrorCS"),sQuery(id+"F2.wireOp",EDGE,"E85.MirrorCS"),sQuery(id+"F2.wireOp",EDGE,"E90.MirrorCS"),sQuery(id+"F2.wireOp",EDGE,"E93.MirrorC"),sQuery(id+"F2.wireOp",EDGE,"E94.MirrorCS")])]});
            booleanBodies(context, id + "F12", {"operationType" : BooleanOperationType.SUBTRACTION, "tools" : qUnion([Q0]), "targets" : qUnion([Q1, Q2]), "keepTools" : true});
        }
        {
            var Q0;
            Q0=makeQuery(id+"F6.opExtrude","CAP_FACE",FACE,{"disambiguationData":[OSD([sQuery(id+"F5.wireOp",EDGE,"E96.0"),sQuery(id+"F5.wireOp",EDGE,"E97.0"),sQuery(id+"F5.wireOp",EDGE,"E98.0"),sQuery(id+"F5.wireOp",EDGE,"E99.0"),sQuery(id+"F5.wireOp",EDGE,"E100.0"),sQuery(id+"F5.wireOp",EDGE,"E101.0"),sQuery(id+"F5.wireOp",EDGE,"E102.0"),sQuery(id+"F5.wireOp",EDGE,"E103.0"),sQuery(id+"F5.wireOp",EDGE,"E104.0"),sQuery(id+"F5.wireOp",EDGE,"E105.0"),sQuery(id+"F5.wireOp",EDGE,"E106"),sQuery(id+"F5.wireOp",EDGE,"E107.1.0.0"),sQuery(id+"F5.wireOp",EDGE,"E107.2.0.0"),sQuery(id+"F5.wireOp",EDGE,"E109.0"),sQuery(id+"F5.wireOp",EDGE,"E110.0"),sQuery(id+"F5.wireOp",EDGE,"E111.0"),sQuery(id+"F5.wireOp",EDGE,"E112.0"),sQuery(id+"F5.wireOp",EDGE,"E112.1"),sQuery(id+"F5.wireOp",EDGE,"E112.2"),sQuery(id+"F5.wireOp",EDGE,"E112.3"),sQuery(id+"F5.wireOp",EDGE,"E113.MirrorC"),sQuery(id+"F5.wireOp",EDGE,"E114.MirrorC"),sQuery(id+"F5.wireOp",EDGE,"E115.MirrorC"),sQuery(id+"F5.wireOp",EDGE,"E116.MirrorC"),sQuery(id+"F5.wireOp",EDGE,"E117.MirrorC"),sQuery(id+"F5.wireOp",EDGE,"E118.MirrorC"),sQuery(id+"F5.wireOp",EDGE,"E119.MirrorC"),sQuery(id+"F5.wireOp",EDGE,"E120.MirrorCS"),sQuery(id+"F5.wireOp",EDGE,"E122.MirrorCS"),sQuery(id+"F5.wireOp",EDGE,"E123.MirrorCS"),sQuery(id+"F5.wireOp",EDGE,"E124.MirrorCS"),sQuery(id+"F5.wireOp",EDGE,"E125.MirrorCS"),sQuery(id+"F5.wireOp",EDGE,"E126.MirrorCS"),sQuery(id+"F5.wireOp",EDGE,"E127.MirrorCS"),sQuery(id+"F5.wireOp",EDGE,"E128.MirrorCS"),sQuery(id+"F5.wireOp",EDGE,"E129.MirrorCS"),sQuery(id+"F5.wireOp",EDGE,"E130.MirrorCS"),sQuery(id+"F5.wireOp",EDGE,"E132.MirrorCS")])],"isStart":false});
            var sketch = newSketch(context, id + "F13", { "sketchPlane" : qUnion([Q0])});
            skCircle(sketch, "E276", {"center": v(-232, 58) * mm, "radius": 1.5 * mm});
            skLineSegment(sketch, "E277", {"start": v(-175, 140) * mm, "end": v(-175, -1.5) * mm, "construction": true});
            skPoint(sketch, "E277.endSnap0", {"position": v(-175, -9.05) * mm});
            skLineSegment(sketch, "E278", {"start": v(-372, 70) * mm, "end": v(22, 70) * mm, "construction": true});
            skCircle(sketch, "E279.MirrorC", {"center": v(-118, 58) * mm, "radius": 1.5 * mm});
            skCircle(sketch, "E280.MirrorC", {"center": v(-232, 82) * mm, "radius": 1.5 * mm});
            skCircle(sketch, "E281.MirrorC", {"center": v(-118, 82) * mm, "radius": 1.5 * mm});
            skSolve(sketch);
        }
        {
            var Q0;
            Q0 = qSketchRegion(id + "F13", true);
            extrude(context, id + "F14", {"entities" : qUnion([Q0]), "operationType" : NewBodyOperationType.REMOVE, "endBound" : BoundingType.THROUGH_ALL, "oppositeDirection" : true, "depth" : 25 * mm});
        }
        {
            var Q0;
            Q0=makeQuery(id+"F3.opExtrude","CAP_FACE",FACE,{"disambiguationData":[OSD([sQuery(id+"F0T68XCoUrNjqKc_0.merge.FRI3efolS22JnH9_0.merge.F2le2PEO98lg6xs_0.merge.FXX2dDxdAnKxtOb_1.wireOp",EDGE,"a45bbf6a-1b3a-4c73-aa77-97d7b8075cbb"),sQuery(id+"F2.wireOp",EDGE,"E0"),sQuery(id+"F2.wireOp",EDGE,"E1"),sQuery(id+"F2.wireOp",EDGE,"E3.MirrorCS"),sQuery(id+"F2.wireOp",EDGE,"E4"),sQuery(id+"F2.wireOp",EDGE,"E5.1.0.0"),sQuery(id+"F2.wireOp",EDGE,"E5.1.0.1"),sQuery(id+"F2.wireOp",EDGE,"E5.1.0.2"),sQuery(id+"F2.wireOp",EDGE,"E5.2.0.0"),sQuery(id+"F2.wireOp",EDGE,"E5.2.0.2"),sQuery(id+"F2.wireOp",EDGE,"E6"),sQuery(id+"F2.wireOp",EDGE,"E9"),sQuery(id+"F2.wireOp",EDGE,"E10.1.0.0"),sQuery(id+"F2.wireOp",EDGE,"E10.1.0.1"),sQuery(id+"F2.wireOp",EDGE,"E5.2.0.1"),sQuery(id+"F2.wireOp",EDGE,"E10.2.0.0"),sQuery(id+"F2.wireOp",EDGE,"E10.2.0.1"),sQuery(id+"F2.wireOp",EDGE,"E13"),sQuery(id+"F2.wireOp",EDGE,"E14"),sQuery(id+"F2.wireOp",EDGE,"E15"),sQuery(id+"F2.wireOp",EDGE,"E16"),sQuery(id+"F2.wireOp",EDGE,"E18.MirrorC"),sQuery(id+"F2.wireOp",EDGE,"E17.MirrorC"),sQuery(id+"F2.wireOp",EDGE,"E20.rect.bottom"),sQuery(id+"F2.wireOp",EDGE,"E20.rect.top"),sQuery(id+"F2.wireOp",EDGE,"E20.rect.left"),sQuery(id+"F2.wireOp",EDGE,"E20.rect.right"),sQuery(id+"F2.wireOp",EDGE,"E21.filletArc"),sQuery(id+"F2.wireOp",EDGE,"E22.filletArc"),sQuery(id+"F2.wireOp",EDGE,"E23.filletArc"),sQuery(id+"F2.wireOp",EDGE,"E24.filletArc"),sQuery(id+"F2.wireOp",EDGE,"E25.1.0.0"),sQuery(id+"F2.wireOp",EDGE,"E25.1.0.3"),sQuery(id+"F2.wireOp",EDGE,"E25.1.0.5"),sQuery(id+"F2.wireOp",EDGE,"E25.1.0.8"),sQuery(id+"F2.wireOp",EDGE,"E25.1.0.9"),sQuery(id+"F2.wireOp",EDGE,"E25.1.0.10"),sQuery(id+"F2.wireOp",EDGE,"E25.1.0.11"),sQuery(id+"F2.wireOp",EDGE,"E25.1.0.12"),sQuery(id+"F2.wireOp",EDGE,"E25.2.0.0"),sQuery(id+"F2.wireOp",EDGE,"E25.2.0.3"),sQuery(id+"F2.wireOp",EDGE,"E25.2.0.5"),sQuery(id+"F2.wireOp",EDGE,"E25.2.0.8"),sQuery(id+"F2.wireOp",EDGE,"E25.2.0.9"),sQuery(id+"F2.wireOp",EDGE,"E25.2.0.10"),sQuery(id+"F2.wireOp",EDGE,"E25.2.0.11"),sQuery(id+"F2.wireOp",EDGE,"E25.2.0.12"),sQuery(id+"F2.wireOp",EDGE,"E26.MirrorCS"),sQuery(id+"F2.wireOp",EDGE,"E27.MirrorCS"),sQuery(id+"F2.wireOp",EDGE,"E28.MirrorCS"),sQuery(id+"F2.wireOp",EDGE,"E29.MirrorCS"),sQuery(id+"F2.wireOp",EDGE,"E30.MirrorCS"),sQuery(id+"F2.wireOp",EDGE,"E31.MirrorCS"),sQuery(id+"F2.wireOp",EDGE,"E32.MirrorCS"),sQuery(id+"F2.wireOp",EDGE,"E33.MirrorCS"),sQuery(id+"F2.wireOp",EDGE,"E34.MirrorCS"),sQuery(id+"F2.wireOp",EDGE,"E35.MirrorCS"),sQuery(id+"F2.wireOp",EDGE,"E36.MirrorCS"),sQuery(id+"F2.wireOp",EDGE,"E37.MirrorCS"),sQuery(id+"F2.wireOp",EDGE,"E38.MirrorCS"),sQuery(id+"F2.wireOp",EDGE,"E39.MirrorCS"),sQuery(id+"F2.wireOp",EDGE,"E40.MirrorCS"),sQuery(id+"F2.wireOp",EDGE,"E41.MirrorCS"),sQuery(id+"F2.wireOp",EDGE,"E42.MirrorCS"),sQuery(id+"F2.wireOp",EDGE,"E43.MirrorCS"),sQuery(id+"F2.wireOp",EDGE,"E44.MirrorCS"),sQuery(id+"F2.wireOp",EDGE,"E45.MirrorCS"),sQuery(id+"F2.wireOp",EDGE,"E46.MirrorCS"),sQuery(id+"F2.wireOp",EDGE,"E47.MirrorCS"),sQuery(id+"F2.wireOp",EDGE,"E48.MirrorCS"),sQuery(id+"F2.wireOp",EDGE,"E49.MirrorC"),sQuery(id+"F2.wireOp",EDGE,"E50.MirrorC"),sQuery(id+"F2.wireOp",EDGE,"E51.MirrorC"),sQuery(id+"F2.wireOp",EDGE,"E52.MirrorC"),sQuery(id+"F2.wireOp",EDGE,"E54.MirrorC"),sQuery(id+"F2.wireOp",EDGE,"E55.MirrorC"),sQuery(id+"F2.wireOp",EDGE,"E57.MirrorC"),sQuery(id+"F2.wireOp",EDGE,"E64.MirrorCS"),sQuery(id+"F2.wireOp",EDGE,"E65.MirrorCS"),sQuery(id+"F2.wireOp",EDGE,"E67.MirrorCS"),sQuery(id+"F2.wireOp",EDGE,"E68.MirrorC"),sQuery(id+"F2.wireOp",EDGE,"E71.MirrorCS"),sQuery(id+"F2.wireOp",EDGE,"E73.MirrorC"),sQuery(id+"F2.wireOp",EDGE,"E75.MirrorCS"),sQuery(id+"F2.wireOp",EDGE,"E76.MirrorCS"),sQuery(id+"F2.wireOp",EDGE,"E79.MirrorCS"),sQuery(id+"F2.wireOp",EDGE,"E81.MirrorCS"),sQuery(id+"F2.wireOp",EDGE,"E83.MirrorCS"),sQuery(id+"F2.wireOp",EDGE,"E84.MirrorCS"),sQuery(id+"F2.wireOp",EDGE,"E53.MirrorCS"),sQuery(id+"F2.wireOp",EDGE,"E85.MirrorCS"),sQuery(id+"F2.wireOp",EDGE,"E90.MirrorCS"),sQuery(id+"F2.wireOp",EDGE,"E93.MirrorC"),sQuery(id+"F2.wireOp",EDGE,"E94.MirrorCS")])],"isStart":false});
            var sketch = newSketch(context, id + "F15", { "sketchPlane" : qUnion([Q0]), "asVersion" : FeatureScriptVersionNumber.V376_FS_VERSION_BUMP});
            skLineSegment(sketch, "E282.0.0", {"start": v(22, -20) * mm, "end": v(7.84, 4.53) * mm});
            skArc(sketch, "E282.0.1", {"start": v(7.84, 4.53) * mm, "mid": v(0, 9.05) * mm, "end": v(-7.84, 4.53) * mm});
            skLineSegment(sketch, "E282.0.2", {"start": v(-7.84, 4.53) * mm, "end": v(-22, -20) * mm});
            skLineSegment(sketch, "E282.0.3", {"start": v(-22, -20) * mm, "end": v(-153, -20) * mm});
            skLineSegment(sketch, "E282.0.4", {"start": v(-153, -20) * mm, "end": v(-167.16, 4.53) * mm});
            skArc(sketch, "E282.0.5", {"start": v(-167.16, 4.53) * mm, "mid": v(-175, 9.05) * mm, "end": v(-182.84, 4.53) * mm});
            skLineSegment(sketch, "E282.0.6", {"start": v(-182.84, 4.53) * mm, "end": v(-197, -20) * mm});
            skLineSegment(sketch, "E282.0.7", {"start": v(-197, -20) * mm, "end": v(-328, -20) * mm});
            skLineSegment(sketch, "E282.0.8", {"start": v(-328, -20) * mm, "end": v(-342.16, 4.53) * mm});
            skArc(sketch, "E282.0.9", {"start": v(-342.16, 4.53) * mm, "mid": v(-350, 9.05) * mm, "end": v(-357.84, 4.53) * mm});
            skLineSegment(sketch, "E282.0.10", {"start": v(-357.84, 4.53) * mm, "end": v(-372, -20) * mm});
            skLineSegment(sketch, "E282.0.11", {"start": v(-372, -20) * mm, "end": v(-372, -120) * mm});
            skLineSegment(sketch, "E282.0.12", {"start": v(-372, -120) * mm, "end": v(-357.84, -144.53) * mm});
            skArc(sketch, "E282.0.13", {"start": v(-357.84, -144.53) * mm, "mid": v(-350, -149.05) * mm, "end": v(-342.16, -144.53) * mm});
            skLineSegment(sketch, "E282.0.14", {"start": v(-342.16, -144.53) * mm, "end": v(-328, -120) * mm});
            skLineSegment(sketch, "E282.0.15", {"start": v(-328, -120) * mm, "end": v(-197, -120) * mm});
            skLineSegment(sketch, "E282.0.16", {"start": v(-197, -120) * mm, "end": v(-182.84, -144.53) * mm});
            skArc(sketch, "E282.0.17", {"start": v(-182.84, -144.53) * mm, "mid": v(-175, -149.05) * mm, "end": v(-167.16, -144.53) * mm});
            skLineSegment(sketch, "E282.0.18", {"start": v(-167.16, -144.53) * mm, "end": v(-153, -120) * mm});
            skLineSegment(sketch, "E282.0.19", {"start": v(-153, -120) * mm, "end": v(-22, -120) * mm});
            skLineSegment(sketch, "E282.0.20", {"start": v(-22, -120) * mm, "end": v(-7.84, -144.53) * mm});
            skArc(sketch, "E282.0.21", {"start": v(-7.84, -144.53) * mm, "mid": v(0, -149.05) * mm, "end": v(7.84, -144.53) * mm});
            skLineSegment(sketch, "E282.0.22", {"start": v(7.84, -144.53) * mm, "end": v(22, -120) * mm});
            skLineSegment(sketch, "E282.0.23", {"start": v(22, -120) * mm, "end": v(22, -20) * mm});
            skCircle(sketch, "E283.0", {"center": v(-350, 0) * mm, "radius": 5.4 * mm});
            skCircle(sketch, "E284.0", {"center": v(-350, -27.43) * mm, "radius": 1.5 * mm});
            skLineSegment(sketch, "E285.0", {"start": v(-346.5, -39) * mm, "end": v(-353.5, -39) * mm});
            skLineSegment(sketch, "E286.0", {"start": v(-354.5, -46) * mm, "end": v(-354.5, -40) * mm});
            skLineSegment(sketch, "E286.1", {"start": v(-346.5, -47) * mm, "end": v(-353.5, -47) * mm});
            skLineSegment(sketch, "E286.2", {"start": v(-345.5, -46) * mm, "end": v(-345.5, -40) * mm});
            skArc(sketch, "E286.3", {"start": v(-345.5, -40) * mm, "mid": v(-345.8, -39.3) * mm, "end": v(-346.5, -39) * mm});
            skArc(sketch, "E286.5", {"start": v(-354.5, -46) * mm, "mid": v(-354.2, -46.7) * mm, "end": v(-353.5, -47) * mm});
            skArc(sketch, "E286.7", {"start": v(-353.5, -39) * mm, "mid": v(-354.2, -39.3) * mm, "end": v(-354.5, -40) * mm});
            skArc(sketch, "E286.8", {"start": v(-346.5, -47) * mm, "mid": v(-345.8, -46.7) * mm, "end": v(-345.5, -46) * mm});
            skArc(sketch, "E286.11", {"start": v(-354.5, -46) * mm, "mid": v(-354.2, -46.7) * mm, "end": v(-353.5, -47) * mm});
            skLineSegment(sketch, "E286.13", {"start": v(-354.5, -46) * mm, "end": v(-354.5, -40) * mm});
            skLineSegment(sketch, "E286.14", {"start": v(-346.5, -47) * mm, "end": v(-353.5, -47) * mm});
            skArc(sketch, "E286.15", {"start": v(-345.5, -40) * mm, "mid": v(-345.8, -39.3) * mm, "end": v(-346.5, -39) * mm});
            skLineSegment(sketch, "E286.18", {"start": v(-345.5, -46) * mm, "end": v(-345.5, -40) * mm});
            skArc(sketch, "E286.19", {"start": v(-353.5, -39) * mm, "mid": v(-354.2, -39.3) * mm, "end": v(-354.5, -40) * mm});
            skArc(sketch, "E286.22", {"start": v(-346.5, -47) * mm, "mid": v(-345.8, -46.7) * mm, "end": v(-345.5, -46) * mm});
            skLineSegment(sketch, "E287.0", {"start": v(-346.5, -93) * mm, "end": v(-353.5, -93) * mm});
            skLineSegment(sketch, "E287.1", {"start": v(-345.5, -94) * mm, "end": v(-345.5, -100) * mm});
            skArc(sketch, "E287.2", {"start": v(-354.5, -94) * mm, "mid": v(-354.2, -93.3) * mm, "end": v(-353.5, -93) * mm});
            skLineSegment(sketch, "E287.3", {"start": v(-354.5, -94) * mm, "end": v(-354.5, -100) * mm});
            skLineSegment(sketch, "E287.5", {"start": v(-346.5, -101) * mm, "end": v(-353.5, -101) * mm});
            skArc(sketch, "E287.6", {"start": v(-346.5, -93) * mm, "mid": v(-345.8, -93.3) * mm, "end": v(-345.5, -94) * mm});
            skArc(sketch, "E287.7", {"start": v(-353.5, -101) * mm, "mid": v(-354.2, -100.7) * mm, "end": v(-354.5, -100) * mm});
            skArc(sketch, "E287.9", {"start": v(-345.5, -100) * mm, "mid": v(-345.8, -100.7) * mm, "end": v(-346.5, -101) * mm});
            skLineSegment(sketch, "E287.13", {"start": v(-346.5, -101) * mm, "end": v(-353.5, -101) * mm});
            skArc(sketch, "E287.14", {"start": v(-346.5, -93) * mm, "mid": v(-345.8, -93.3) * mm, "end": v(-345.5, -94) * mm});
            skLineSegment(sketch, "E287.16", {"start": v(-346.5, -93) * mm, "end": v(-353.5, -93) * mm});
            skLineSegment(sketch, "E287.17", {"start": v(-345.5, -94) * mm, "end": v(-345.5, -100) * mm});
            skArc(sketch, "E287.20", {"start": v(-354.5, -94) * mm, "mid": v(-354.2, -93.3) * mm, "end": v(-353.5, -93) * mm});
            skArc(sketch, "E287.21", {"start": v(-353.5, -101) * mm, "mid": v(-354.2, -100.7) * mm, "end": v(-354.5, -100) * mm});
            skLineSegment(sketch, "E287.22", {"start": v(-354.5, -94) * mm, "end": v(-354.5, -100) * mm});
            skArc(sketch, "E287.23", {"start": v(-345.5, -100) * mm, "mid": v(-345.8, -100.7) * mm, "end": v(-346.5, -101) * mm});
            skCircle(sketch, "E288.0", {"center": v(-350, -112.57) * mm, "radius": 1.5 * mm});
            skCircle(sketch, "E289.0", {"center": v(-350, -140) * mm, "radius": 5.4 * mm});
            skCircle(sketch, "E290.0", {"center": v(-282.5, -115) * mm, "radius": 1.5 * mm});
            skCircle(sketch, "E291.0", {"center": v(-242.5, -115) * mm, "radius": 1.5 * mm});
            skCircle(sketch, "E292.0", {"center": v(-282.5, -25) * mm, "radius": 1.5 * mm});
            skCircle(sketch, "E293.0", {"center": v(-242.5, -25) * mm, "radius": 1.5 * mm});
            skCircle(sketch, "E294.0", {"center": v(-175, -27.43) * mm, "radius": 1.5 * mm});
            skCircle(sketch, "E295.0", {"center": v(-175, 0) * mm, "radius": 5.4 * mm});
            skCircle(sketch, "E296.0", {"center": v(-175, -140) * mm, "radius": 5.4 * mm});
            skCircle(sketch, "E297.0", {"center": v(-175, -112.57) * mm, "radius": 1.5 * mm});
            skLineSegment(sketch, "E298.0", {"start": v(-171.5, -93) * mm, "end": v(-178.5, -93) * mm});
            skLineSegment(sketch, "E298.1", {"start": v(-171.5, -101) * mm, "end": v(-178.5, -101) * mm});
            skLineSegment(sketch, "E298.2", {"start": v(-171.5, -101) * mm, "end": v(-178.5, -101) * mm});
            skLineSegment(sketch, "E298.3", {"start": v(-171.5, -93) * mm, "end": v(-178.5, -93) * mm});
            skLineSegment(sketch, "E298.4", {"start": v(-179.5, -94) * mm, "end": v(-179.5, -100) * mm});
            skArc(sketch, "E298.5", {"start": v(-170.5, -100) * mm, "mid": v(-170.8, -100.7) * mm, "end": v(-171.5, -101) * mm});
            skLineSegment(sketch, "E298.6", {"start": v(-170.5, -94) * mm, "end": v(-170.5, -100) * mm});
            skArc(sketch, "E298.8", {"start": v(-171.5, -93) * mm, "mid": v(-170.8, -93.3) * mm, "end": v(-170.5, -94) * mm});
            skArc(sketch, "E298.9", {"start": v(-178.5, -101) * mm, "mid": v(-179.2, -100.7) * mm, "end": v(-179.5, -100) * mm});
            skArc(sketch, "E298.10", {"start": v(-179.5, -94) * mm, "mid": v(-179.2, -93.3) * mm, "end": v(-178.5, -93) * mm});
            skLineSegment(sketch, "E298.12", {"start": v(-179.5, -94) * mm, "end": v(-179.5, -100) * mm});
            skArc(sketch, "E298.18", {"start": v(-171.5, -93) * mm, "mid": v(-170.8, -93.3) * mm, "end": v(-170.5, -94) * mm});
            skLineSegment(sketch, "E298.19", {"start": v(-170.5, -94) * mm, "end": v(-170.5, -100) * mm});
            skArc(sketch, "E298.20", {"start": v(-170.5, -100) * mm, "mid": v(-170.8, -100.7) * mm, "end": v(-171.5, -101) * mm});
            skArc(sketch, "E298.22", {"start": v(-178.5, -101) * mm, "mid": v(-179.2, -100.7) * mm, "end": v(-179.5, -100) * mm});
            skArc(sketch, "E298.23", {"start": v(-179.5, -94) * mm, "mid": v(-179.2, -93.3) * mm, "end": v(-178.5, -93) * mm});
            skLineSegment(sketch, "E299.0", {"start": v(-171.5, -39) * mm, "end": v(-178.5, -39) * mm});
            skLineSegment(sketch, "E299.1", {"start": v(-179.5, -46) * mm, "end": v(-179.5, -40) * mm});
            skLineSegment(sketch, "E299.2", {"start": v(-171.5, -47) * mm, "end": v(-178.5, -47) * mm});
            skLineSegment(sketch, "E299.3", {"start": v(-170.5, -46) * mm, "end": v(-170.5, -40) * mm});
            skArc(sketch, "E299.4", {"start": v(-170.5, -40) * mm, "mid": v(-170.8, -39.3) * mm, "end": v(-171.5, -39) * mm});
            skArc(sketch, "E299.5", {"start": v(-179.5, -46) * mm, "mid": v(-179.2, -46.7) * mm, "end": v(-178.5, -47) * mm});
            skArc(sketch, "E299.6", {"start": v(-178.5, -39) * mm, "mid": v(-179.2, -39.3) * mm, "end": v(-179.5, -40) * mm});
            skLineSegment(sketch, "E299.7", {"start": v(-171.5, -39) * mm, "end": v(-178.5, -39) * mm});
            skArc(sketch, "E299.9", {"start": v(-171.5, -47) * mm, "mid": v(-170.8, -46.7) * mm, "end": v(-170.5, -46) * mm});
            skArc(sketch, "E299.11", {"start": v(-179.5, -46) * mm, "mid": v(-179.2, -46.7) * mm, "end": v(-178.5, -47) * mm});
            skLineSegment(sketch, "E299.13", {"start": v(-179.5, -46) * mm, "end": v(-179.5, -40) * mm});
            skLineSegment(sketch, "E299.16", {"start": v(-171.5, -47) * mm, "end": v(-178.5, -47) * mm});
            skArc(sketch, "E299.18", {"start": v(-170.5, -40) * mm, "mid": v(-170.8, -39.3) * mm, "end": v(-171.5, -39) * mm});
            skLineSegment(sketch, "E299.20", {"start": v(-170.5, -46) * mm, "end": v(-170.5, -40) * mm});
            skArc(sketch, "E299.22", {"start": v(-178.5, -39) * mm, "mid": v(-179.2, -39.3) * mm, "end": v(-179.5, -40) * mm});
            skArc(sketch, "E299.23", {"start": v(-171.5, -47) * mm, "mid": v(-170.8, -46.7) * mm, "end": v(-170.5, -46) * mm});
            skLineSegment(sketch, "E300.0", {"start": v(-4.5, -46) * mm, "end": v(-4.5, -40) * mm});
            skLineSegment(sketch, "E300.1", {"start": v(4.5, -46) * mm, "end": v(4.5, -40) * mm});
            skLineSegment(sketch, "E300.2", {"start": v(3.5, -39) * mm, "end": v(-3.5, -39) * mm});
            skArc(sketch, "E300.3", {"start": v(4.5, -40) * mm, "mid": v(4.2, -39.3) * mm, "end": v(3.5, -39) * mm});
            skArc(sketch, "E300.4", {"start": v(-3.5, -39) * mm, "mid": v(-4.2, -39.3) * mm, "end": v(-4.5, -40) * mm});
            skLineSegment(sketch, "E300.5", {"start": v(3.5, -47) * mm, "end": v(-3.5, -47) * mm});
            skArc(sketch, "E300.7", {"start": v(3.5, -47) * mm, "mid": v(4.2, -46.7) * mm, "end": v(4.5, -46) * mm});
            skArc(sketch, "E300.10", {"start": v(-4.5, -46) * mm, "mid": v(-4.2, -46.7) * mm, "end": v(-3.5, -47) * mm});
            skArc(sketch, "E300.16", {"start": v(-3.5, -39) * mm, "mid": v(-4.2, -39.3) * mm, "end": v(-4.5, -40) * mm});
            skLineSegment(sketch, "E300.17", {"start": v(-4.5, -46) * mm, "end": v(-4.5, -40) * mm});
            skLineSegment(sketch, "E300.18", {"start": v(4.5, -46) * mm, "end": v(4.5, -40) * mm});
            skArc(sketch, "E300.19", {"start": v(4.5, -40) * mm, "mid": v(4.2, -39.3) * mm, "end": v(3.5, -39) * mm});
            skLineSegment(sketch, "E300.20", {"start": v(3.5, -39) * mm, "end": v(-3.5, -39) * mm});
            skArc(sketch, "E300.21", {"start": v(3.5, -47) * mm, "mid": v(4.2, -46.7) * mm, "end": v(4.5, -46) * mm});
            skLineSegment(sketch, "E300.22", {"start": v(3.5, -47) * mm, "end": v(-3.5, -47) * mm});
            skArc(sketch, "E300.23", {"start": v(-4.5, -46) * mm, "mid": v(-4.2, -46.7) * mm, "end": v(-3.5, -47) * mm});
            skLineSegment(sketch, "E301.0", {"start": v(-4.5, -94) * mm, "end": v(-4.5, -100) * mm});
            skArc(sketch, "E301.1", {"start": v(3.5, -93) * mm, "mid": v(4.2, -93.3) * mm, "end": v(4.5, -94) * mm});
            skArc(sketch, "E301.2", {"start": v(4.5, -100) * mm, "mid": v(4.2, -100.7) * mm, "end": v(3.5, -101) * mm});
            skLineSegment(sketch, "E301.3", {"start": v(3.5, -93) * mm, "end": v(-3.5, -93) * mm});
            skArc(sketch, "E301.4", {"start": v(-4.5, -94) * mm, "mid": v(-4.2, -93.3) * mm, "end": v(-3.5, -93) * mm});
            skLineSegment(sketch, "E301.7", {"start": v(3.5, -101) * mm, "end": v(-3.5, -101) * mm});
            skLineSegment(sketch, "E301.8", {"start": v(4.5, -94) * mm, "end": v(4.5, -100) * mm});
            skArc(sketch, "E301.11", {"start": v(-3.5, -101) * mm, "mid": v(-4.2, -100.7) * mm, "end": v(-4.5, -100) * mm});
            skLineSegment(sketch, "E301.15", {"start": v(-4.5, -94) * mm, "end": v(-4.5, -100) * mm});
            skArc(sketch, "E301.16", {"start": v(4.5, -100) * mm, "mid": v(4.2, -100.7) * mm, "end": v(3.5, -101) * mm});
            skArc(sketch, "E301.17", {"start": v(3.5, -93) * mm, "mid": v(4.2, -93.3) * mm, "end": v(4.5, -94) * mm});
            skLineSegment(sketch, "E301.18", {"start": v(3.5, -101) * mm, "end": v(-3.5, -101) * mm});
            skLineSegment(sketch, "E301.20", {"start": v(3.5, -93) * mm, "end": v(-3.5, -93) * mm});
            skArc(sketch, "E301.21", {"start": v(-4.5, -94) * mm, "mid": v(-4.2, -93.3) * mm, "end": v(-3.5, -93) * mm});
            skArc(sketch, "E301.22", {"start": v(-3.5, -101) * mm, "mid": v(-4.2, -100.7) * mm, "end": v(-4.5, -100) * mm});
            skLineSegment(sketch, "E301.23", {"start": v(4.5, -94) * mm, "end": v(4.5, -100) * mm});
            skCircle(sketch, "E302.0", {"center": v(0, -140) * mm, "radius": 5.4 * mm});
            skCircle(sketch, "E303.0", {"center": v(0, -112.57) * mm, "radius": 1.5 * mm});
            skCircle(sketch, "E304.0", {"center": v(0, -27.43) * mm, "radius": 1.5 * mm});
            skCircle(sketch, "E305.0", {"center": v(0, 0) * mm, "radius": 5.55 * mm});
            skCircle(sketch, "E306.0", {"center": v(-50.25, -32.75) * mm, "radius": 1.5 * mm});
            skCircle(sketch, "E307.0", {"center": v(-67.5, -25) * mm, "radius": 1.5 * mm});
            skCircle(sketch, "E308.0", {"center": v(-107.5, -25) * mm, "radius": 1.5 * mm});
            skCircle(sketch, "E309.0", {"center": v(-124.75, -32.75) * mm, "radius": 1.5 * mm});
            skCircle(sketch, "E310.0", {"center": v(-124.75, -107.25) * mm, "radius": 1.5 * mm});
            skCircle(sketch, "E311.0", {"center": v(-107.5, -115) * mm, "radius": 1.5 * mm});
            skCircle(sketch, "E312.0", {"center": v(-67.5, -115) * mm, "radius": 1.5 * mm});
            skCircle(sketch, "E313.0", {"center": v(-50.25, -107.25) * mm, "radius": 1.5 * mm});
            skLineSegment(sketch, "E314", {"start": v(-87.5, -20) * mm, "end": v(-87.5, -120) * mm, "construction": true});
            skLineSegment(sketch, "E315.0.0", {"start": v(-338, -73) * mm, "end": v(-318, -73) * mm});
            skLineSegment(sketch, "E315.0.1", {"start": v(-318, -73) * mm, "end": v(-318, -67) * mm});
            skLineSegment(sketch, "E315.0.2", {"start": v(-318, -67) * mm, "end": v(-338, -67) * mm});
            skLineSegment(sketch, "E315.0.3", {"start": v(-338, -67) * mm, "end": v(-338, -73) * mm});
            skLineSegment(sketch, "E316.0.0", {"start": v(-207, -73) * mm, "end": v(-187, -73) * mm});
            skLineSegment(sketch, "E316.0.1", {"start": v(-187, -73) * mm, "end": v(-187, -67) * mm});
            skLineSegment(sketch, "E316.0.2", {"start": v(-187, -67) * mm, "end": v(-207, -67) * mm});
            skLineSegment(sketch, "E316.0.3", {"start": v(-207, -67) * mm, "end": v(-207, -73) * mm});
            skLineSegment(sketch, "E317.0.0", {"start": v(-163, -73) * mm, "end": v(-143, -73) * mm});
            skLineSegment(sketch, "E317.0.1", {"start": v(-143, -73) * mm, "end": v(-143, -67) * mm});
            skLineSegment(sketch, "E317.0.2", {"start": v(-143, -67) * mm, "end": v(-163, -67) * mm});
            skLineSegment(sketch, "E317.0.3", {"start": v(-163, -67) * mm, "end": v(-163, -73) * mm});
            skLineSegment(sketch, "E318.0.0", {"start": v(-32, -73) * mm, "end": v(-12, -73) * mm});
            skLineSegment(sketch, "E318.0.1", {"start": v(-12, -73) * mm, "end": v(-12, -67) * mm});
            skLineSegment(sketch, "E318.0.2", {"start": v(-12, -67) * mm, "end": v(-32, -67) * mm});
            skLineSegment(sketch, "E318.0.3", {"start": v(-32, -67) * mm, "end": v(-32, -73) * mm});
            skPoint(sketch, "E319.0", {"position": v(5, -67) * mm});
            skPoint(sketch, "E320.0", {"position": v(5, -73) * mm});
            skPoint(sketch, "E321.0", {"position": v(-355, -67) * mm});
            skPoint(sketch, "E322.0", {"position": v(-355, -73) * mm});
            skPoint(sketch, "E323.0", {"position": v(-175, -67) * mm});
            skPoint(sketch, "E324.0", {"position": v(-175, -73) * mm});
            skLineSegment(sketch, "E325", {"start": v(-355, -67) * mm, "end": v(-355, -73) * mm, "construction": true});
            skLineSegment(sketch, "E326", {"start": v(-175, -67) * mm, "end": v(-175, -73) * mm, "construction": true});
            skLineSegment(sketch, "E327", {"start": v(5, -67) * mm, "end": v(5, -73) * mm, "construction": true});
            skCircle(sketch, "E328", {"center": v(5, -70) * mm, "radius": 1.5 * mm});
            skCircle(sketch, "E329", {"center": v(-175, -70) * mm, "radius": 1.5 * mm});
            skCircle(sketch, "E330", {"center": v(-355, -70) * mm, "radius": 1.5 * mm});
            skLineSegment(sketch, "E331.bottom", {"start": v(-77.5, -95) * mm, "end": v(-97.5, -95) * mm});
            skLineSegment(sketch, "E331.top", {"start": v(-77.5, -45) * mm, "end": v(-97.5, -45) * mm});
            skLineSegment(sketch, "E331.left", {"start": v(-67.5, -85) * mm, "end": v(-67.5, -55) * mm});
            skLineSegment(sketch, "E331.right", {"start": v(-107.5, -85) * mm, "end": v(-107.5, -55) * mm});
            skPoint(sketch, "E331.middle", {"position": v(-87.5, -70) * mm});
            skPoint(sketch, "E332.visualSharp", {"position": v(-107.5, -45) * mm});
            skArc(sketch, "E332.filletArc", {"start": v(-97.5, -45) * mm, "mid": v(-104.57, -47.93) * mm, "end": v(-107.5, -55) * mm});
            skPoint(sketch, "E333.visualSharp", {"position": v(-67.5, -45) * mm});
            skArc(sketch, "E333.filletArc", {"start": v(-67.5, -55) * mm, "mid": v(-70.43, -47.93) * mm, "end": v(-77.5, -45) * mm});
            skPoint(sketch, "E334.visualSharp", {"position": v(-67.5, -95) * mm});
            skArc(sketch, "E334.filletArc", {"start": v(-77.5, -95) * mm, "mid": v(-70.43, -92.07) * mm, "end": v(-67.5, -85) * mm});
            skPoint(sketch, "E335.visualSharp", {"position": v(-107.5, -95) * mm});
            skArc(sketch, "E335.filletArc", {"start": v(-107.5, -85) * mm, "mid": v(-104.57, -92.07) * mm, "end": v(-97.5, -95) * mm});
            skCircle(sketch, "E336.0", {"center": v(-232, -58) * mm, "radius": 1.5 * mm});
            skCircle(sketch, "E337.0", {"center": v(-232, -82) * mm, "radius": 1.5 * mm});
            skCircle(sketch, "E338.0", {"center": v(-118, -82) * mm, "radius": 1.5 * mm});
            skCircle(sketch, "E339.0", {"center": v(-118, -58) * mm, "radius": 1.5 * mm});
            skSolve(sketch);
        }
        {
            var Q0;
            Q0=makeQuery(id+"F15.imprint","IMPRINT",FACE,{"disambiguationData":[TD([[makeQuery(id+"F15.imprint","IMPRINT",EDGE,{"derivedFrom":sQuery(id+"F15.wireOp",EDGE,"E330")}),1.0]])]});
            var Q1;
            Q1=makeQuery(id+"F15.imprint","IMPRINT",FACE,{"disambiguationData":[TD([[makeQuery(id+"F15.imprint","IMPRINT",EDGE,{"derivedFrom":sQuery(id+"F15.wireOp",EDGE,"E329")}),1.0]])]});
            var Q2;
            Q2=makeQuery(id+"F15.imprint","IMPRINT",FACE,{"disambiguationData":[TD([[makeQuery(id+"F15.imprint","IMPRINT",EDGE,{"derivedFrom":sQuery(id+"F15.wireOp",EDGE,"E328")}),1.0]])]});
            var Q3;
            Q3=makeQuery(id+"F15.imprint","IMPRINT",FACE,{"disambiguationData":[TD([[makeQuery(id+"F15.imprint","IMPRINT",EDGE,{"derivedFrom":sQuery(id+"F15.wireOp",EDGE,"E331.bottom")}),-1.0]])]});
            extrude(context, id + "F16", {"entities" : qUnion([Q0, Q1, Q2, Q3]), "operationType" : NewBodyOperationType.REMOVE, "endBound" : BoundingType.UP_TO_NEXT, "oppositeDirection" : true, "depth" : 25 * mm});
        }
        {
            var Q0;
            Q0=makeQuery(id+"F11.opExtrude","CAP_FACE",FACE,{"disambiguationData":[OSD([sQuery(id+"F10.wireOp",EDGE,"E147"),sQuery(id+"F10.wireOp",EDGE,"E148"),sQuery(id+"F10.wireOp",EDGE,"E150.top"),sQuery(id+"F10.wireOp",EDGE,"E150.left"),sQuery(id+"F10.wireOp",EDGE,"E150.right"),sQuery(id+"F10.wireOp",EDGE,"E151.bottom"),sQuery(id+"F10.wireOp",EDGE,"E151.top"),sQuery(id+"F10.wireOp",EDGE,"E151.left"),sQuery(id+"F10.wireOp",EDGE,"E151.right"),sQuery(id+"F10.wireOp",EDGE,"E152.trimOffspring"),sQuery(id+"F10.wireOp",EDGE,"E153.trimOffspring"),sQuery(id+"F10.wireOp",EDGE,"E154.trimOffspring"),sQuery(id+"F10.wireOp",EDGE,"E155.trimOffspring"),sQuery(id+"F10.wireOp",EDGE,"E156"),sQuery(id+"F10.wireOp",EDGE,"E157"),sQuery(id+"F10.wireOp",EDGE,"E159"),sQuery(id+"F10.wireOp",EDGE,"E160"),sQuery(id+"F10.wireOp",EDGE,"E161"),sQuery(id+"F10.wireOp",EDGE,"E165"),sQuery(id+"F10.wireOp",EDGE,"E166"),sQuery(id+"F10.wireOp",EDGE,"E167"),sQuery(id+"F10.wireOp",EDGE,"E168"),sQuery(id+"F10.wireOp",EDGE,"E169"),sQuery(id+"F10.wireOp",EDGE,"E170"),sQuery(id+"F10.wireOp",EDGE,"E171"),sQuery(id+"F10.wireOp",EDGE,"E172"),sQuery(id+"F10.wireOp",EDGE,"E173"),sQuery(id+"F10.wireOp",EDGE,"E174.1.0.0"),sQuery(id+"F10.wireOp",EDGE,"E174.1.0.1"),sQuery(id+"F10.wireOp",EDGE,"E174.1.0.3"),sQuery(id+"F10.wireOp",EDGE,"E174.1.0.4"),sQuery(id+"F10.wireOp",EDGE,"E174.1.0.5"),sQuery(id+"F10.wireOp",EDGE,"E174.1.0.6"),sQuery(id+"F10.wireOp",EDGE,"E174.1.0.7"),sQuery(id+"F10.wireOp",EDGE,"E174.1.0.8"),sQuery(id+"F10.wireOp",EDGE,"E174.1.0.9"),sQuery(id+"F10.wireOp",EDGE,"E174.1.0.10"),sQuery(id+"F10.wireOp",EDGE,"E174.1.0.11"),sQuery(id+"F10.wireOp",EDGE,"E174.2.0.0"),sQuery(id+"F10.wireOp",EDGE,"E174.2.0.1"),sQuery(id+"F10.wireOp",EDGE,"E174.2.0.3"),sQuery(id+"F10.wireOp",EDGE,"E174.2.0.4"),sQuery(id+"F10.wireOp",EDGE,"E174.2.0.5"),sQuery(id+"F10.wireOp",EDGE,"E174.2.0.6"),sQuery(id+"F10.wireOp",EDGE,"E174.2.0.7"),sQuery(id+"F10.wireOp",EDGE,"E174.2.0.8"),sQuery(id+"F10.wireOp",EDGE,"E174.2.0.9"),sQuery(id+"F10.wireOp",EDGE,"E174.2.0.10"),sQuery(id+"F10.wireOp",EDGE,"E174.2.0.11"),sQuery(id+"F10.wireOp",EDGE,"E175"),sQuery(id+"F10.wireOp",EDGE,"E176"),sQuery(id+"F10.wireOp",EDGE,"E177"),sQuery(id+"F10.wireOp",EDGE,"E178"),sQuery(id+"F10.wireOp",EDGE,"E179"),sQuery(id+"F10.wireOp",EDGE,"E180"),sQuery(id+"F10.wireOp",EDGE,"E181.MirrorCS"),sQuery(id+"F10.wireOp",EDGE,"E182.MirrorCS"),sQuery(id+"F10.wireOp",EDGE,"E183.MirrorCS"),sQuery(id+"F10.wireOp",EDGE,"E184.MirrorCS"),sQuery(id+"F10.wireOp",EDGE,"E185.MirrorCS"),sQuery(id+"F10.wireOp",EDGE,"E186.MirrorCS"),sQuery(id+"F10.wireOp",EDGE,"E187.MirrorCS"),sQuery(id+"F10.wireOp",EDGE,"E188.MirrorCS"),sQuery(id+"F10.wireOp",EDGE,"E189.MirrorCS"),sQuery(id+"F10.wireOp",EDGE,"E190.MirrorCS"),sQuery(id+"F10.wireOp",EDGE,"E191.MirrorCS"),sQuery(id+"F10.wireOp",EDGE,"E192.MirrorCS"),sQuery(id+"F10.wireOp",EDGE,"E193.MirrorCS"),sQuery(id+"F10.wireOp",EDGE,"E194.MirrorCS"),sQuery(id+"F10.wireOp",EDGE,"E195.MirrorCS"),sQuery(id+"F10.wireOp",EDGE,"E196.MirrorCS"),sQuery(id+"F10.wireOp",EDGE,"E197.MirrorCS"),sQuery(id+"F10.wireOp",EDGE,"E198.MirrorCS"),sQuery(id+"F10.wireOp",EDGE,"E199.MirrorCS"),sQuery(id+"F10.wireOp",EDGE,"E200.MirrorCS"),sQuery(id+"F10.wireOp",EDGE,"E201.MirrorCS"),sQuery(id+"F10.wireOp",EDGE,"E202.MirrorCS"),sQuery(id+"F10.wireOp",EDGE,"E203.MirrorCS"),sQuery(id+"F10.wireOp",EDGE,"E204.MirrorCS"),sQuery(id+"F10.wireOp",EDGE,"E205.MirrorCS"),sQuery(id+"F10.wireOp",EDGE,"E206.MirrorCS"),sQuery(id+"F10.wireOp",EDGE,"E207.MirrorCS"),sQuery(id+"F10.wireOp",EDGE,"E208.MirrorCS"),sQuery(id+"F10.wireOp",EDGE,"E209.MirrorCS"),sQuery(id+"F10.wireOp",EDGE,"E210.MirrorCS"),sQuery(id+"F10.wireOp",EDGE,"E211.MirrorCS"),sQuery(id+"F10.wireOp",EDGE,"E212.MirrorCS"),sQuery(id+"F10.wireOp",EDGE,"E213.MirrorCS"),sQuery(id+"F10.wireOp",EDGE,"E214.MirrorCS"),sQuery(id+"F10.wireOp",EDGE,"E215.MirrorCS"),sQuery(id+"F10.wireOp",EDGE,"E216.MirrorCS"),sQuery(id+"F10.wireOp",EDGE,"E217.MirrorCS"),sQuery(id+"F10.wireOp",EDGE,"E218.MirrorCS"),sQuery(id+"F10.wireOp",EDGE,"E219.MirrorCS"),sQuery(id+"F10.wireOp",EDGE,"E220.MirrorCS"),sQuery(id+"F10.wireOp",EDGE,"E222.MirrorCS"),sQuery(id+"F10.wireOp",EDGE,"E223.MirrorCS"),sQuery(id+"F10.wireOp",EDGE,"E224.MirrorCS"),sQuery(id+"F10.wireOp",EDGE,"E225.MirrorCS"),sQuery(id+"F10.wireOp",EDGE,"E226.MirrorCS"),sQuery(id+"F10.wireOp",EDGE,"E230.MirrorCS"),sQuery(id+"F10.wireOp",EDGE,"E232.MirrorCS"),sQuery(id+"F10.wireOp",EDGE,"E233.MirrorCS"),sQuery(id+"F10.wireOp",EDGE,"E234.MirrorCS"),sQuery(id+"F10.wireOp",EDGE,"E237.MirrorCS"),sQuery(id+"F10.wireOp",EDGE,"E239.MirrorCS"),sQuery(id+"F10.wireOp",EDGE,"E241.MirrorCS"),sQuery(id+"F10.wireOp",EDGE,"E242.MirrorCS"),sQuery(id+"F10.wireOp",EDGE,"E246.MirrorCS"),sQuery(id+"F10.wireOp",EDGE,"E247.MirrorCS")])],"isStart":true});
            var sketch = newSketch(context, id + "F17", { "sketchPlane" : qUnion([Q0])});
            skLineSegment(sketch, "E340.left", {"start": v(-338, 0) * mm, "end": v(-338, -46) * mm, "construction": true});
            skLineSegment(sketch, "E340.right", {"start": v(-187, 0) * mm, "end": v(-187, -46) * mm, "construction": true});
            skLineSegment(sketch, "E341", {"start": v(-338, 0) * mm, "end": v(-300.25, -46) * mm, "construction": true});
            skLineSegment(sketch, "E342", {"start": v(-300.25, -46) * mm, "end": v(-262.5, 0) * mm, "construction": true});
            skLineSegment(sketch, "E343", {"start": v(-262.5, 0) * mm, "end": v(-224.75, -46) * mm, "construction": true});
            skLineSegment(sketch, "E344", {"start": v(-224.75, -46) * mm, "end": v(-187, 0) * mm, "construction": true});
            skLineSegment(sketch, "E345", {"start": v(-338, 0) * mm, "end": v(-262.5, 0) * mm, "construction": true});
            skLineSegment(sketch, "E346", {"start": v(-262.5, 0) * mm, "end": v(-187, 0) * mm, "construction": true});
            skLineSegment(sketch, "E347", {"start": v(-338, -46) * mm, "end": v(-300.25, -46) * mm, "construction": true});
            skLineSegment(sketch, "E348", {"start": v(-300.25, -46) * mm, "end": v(-224.75, -46) * mm, "construction": true});
            skLineSegment(sketch, "E349", {"start": v(-224.75, -46) * mm, "end": v(-187, -46) * mm, "construction": true});
            skLineSegment(sketch, "E350.0", {"start": v(-321.09, -5) * mm, "end": v(-279.41, -5) * mm});
            skLineSegment(sketch, "E350.1", {"start": v(-323.4, -9.9) * mm, "end": v(-302.57, -35.3) * mm});
            skLineSegment(sketch, "E350.2", {"start": v(-297.93, -35.3) * mm, "end": v(-277.1, -9.9) * mm});
            skLineSegment(sketch, "E351.0", {"start": v(-327.68, -20.46) * mm, "end": v(-314.85, -36.1) * mm});
            skLineSegment(sketch, "E351.1", {"start": v(-333, -22.36) * mm, "end": v(-333, -38) * mm});
            skLineSegment(sketch, "E351.2", {"start": v(-330, -41) * mm, "end": v(-317.16, -41) * mm});
            skLineSegment(sketch, "E352.0", {"start": v(-285.65, -36.1) * mm, "end": v(-264.82, -10.7) * mm});
            skLineSegment(sketch, "E352.1", {"start": v(-283.34, -41) * mm, "end": v(-241.66, -41) * mm});
            skLineSegment(sketch, "E352.2", {"start": v(-260.18, -10.7) * mm, "end": v(-239.35, -36.1) * mm});
            skLineSegment(sketch, "E353.0", {"start": v(-245.59, -5) * mm, "end": v(-203.91, -5) * mm});
            skLineSegment(sketch, "E353.1", {"start": v(-247.9, -9.9) * mm, "end": v(-227.07, -35.3) * mm});
            skLineSegment(sketch, "E353.2", {"start": v(-222.43, -35.3) * mm, "end": v(-201.6, -9.9) * mm});
            skLineSegment(sketch, "E354.0", {"start": v(-207.84, -41) * mm, "end": v(-195, -41) * mm});
            skLineSegment(sketch, "E354.1", {"start": v(-210.15, -36.1) * mm, "end": v(-197.32, -20.46) * mm});
            skLineSegment(sketch, "E354.2", {"start": v(-192, -22.36) * mm, "end": v(-192, -38) * mm});
            skPoint(sketch, "E355.visualSharp", {"position": v(-327.43, -5) * mm});
            skArc(sketch, "E355.filletArc", {"start": v(-321.09, -5) * mm, "mid": v(-323.8, -6.72) * mm, "end": v(-323.4, -9.9) * mm});
            skPoint(sketch, "E356.visualSharp", {"position": v(-273.07, -5) * mm});
            skArc(sketch, "E356.filletArc", {"start": v(-277.1, -9.9) * mm, "mid": v(-276.7, -6.72) * mm, "end": v(-279.41, -5) * mm});
            skPoint(sketch, "E357.visualSharp", {"position": v(-300.25, -38.12) * mm});
            skArc(sketch, "E357.filletArc", {"start": v(-302.57, -35.3) * mm, "mid": v(-300.25, -36.39) * mm, "end": v(-297.93, -35.3) * mm});
            skPoint(sketch, "E358.visualSharp", {"position": v(-333, -13.97) * mm});
            skArc(sketch, "E358.filletArc", {"start": v(-327.68, -20.46) * mm, "mid": v(-331.01, -19.53) * mm, "end": v(-333, -22.36) * mm});
            skPoint(sketch, "E359.visualSharp", {"position": v(-333, -41) * mm});
            skArc(sketch, "E359.filletArc", {"start": v(-333, -38) * mm, "mid": v(-332.12, -40.12) * mm, "end": v(-330, -41) * mm});
            skPoint(sketch, "E360.visualSharp", {"position": v(-310.82, -41) * mm});
            skArc(sketch, "E360.filletArc", {"start": v(-317.16, -41) * mm, "mid": v(-314.45, -39.28) * mm, "end": v(-314.85, -36.1) * mm});
            skPoint(sketch, "E361.visualSharp", {"position": v(-289.68, -41) * mm});
            skArc(sketch, "E361.filletArc", {"start": v(-285.65, -36.1) * mm, "mid": v(-286.05, -39.28) * mm, "end": v(-283.34, -41) * mm});
            skPoint(sketch, "E362.visualSharp", {"position": v(-262.5, -7.88) * mm});
            skArc(sketch, "E362.filletArc", {"start": v(-260.18, -10.7) * mm, "mid": v(-262.5, -9.61) * mm, "end": v(-264.82, -10.7) * mm});
            skPoint(sketch, "E363.visualSharp", {"position": v(-251.93, -5) * mm});
            skArc(sketch, "E363.filletArc", {"start": v(-245.59, -5) * mm, "mid": v(-248.3, -6.72) * mm, "end": v(-247.9, -9.9) * mm});
            skPoint(sketch, "E364.visualSharp", {"position": v(-235.32, -41) * mm});
            skArc(sketch, "E364.filletArc", {"start": v(-241.66, -41) * mm, "mid": v(-238.95, -39.28) * mm, "end": v(-239.35, -36.1) * mm});
            skPoint(sketch, "E365.visualSharp", {"position": v(-224.75, -38.12) * mm});
            skArc(sketch, "E365.filletArc", {"start": v(-227.07, -35.3) * mm, "mid": v(-224.75, -36.39) * mm, "end": v(-222.43, -35.3) * mm});
            skPoint(sketch, "E366.visualSharp", {"position": v(-197.57, -5) * mm});
            skArc(sketch, "E366.filletArc", {"start": v(-201.6, -9.9) * mm, "mid": v(-201.2, -6.72) * mm, "end": v(-203.91, -5) * mm});
            skPoint(sketch, "E367.visualSharp", {"position": v(-192, -13.97) * mm});
            skArc(sketch, "E367.filletArc", {"start": v(-192, -22.36) * mm, "mid": v(-193.99, -19.53) * mm, "end": v(-197.32, -20.46) * mm});
            skPoint(sketch, "E368.visualSharp", {"position": v(-192, -41) * mm});
            skArc(sketch, "E368.filletArc", {"start": v(-195, -41) * mm, "mid": v(-192.88, -40.12) * mm, "end": v(-192, -38) * mm});
            skPoint(sketch, "E369.visualSharp", {"position": v(-214.18, -41) * mm});
            skArc(sketch, "E369.filletArc", {"start": v(-210.15, -36.1) * mm, "mid": v(-210.55, -39.28) * mm, "end": v(-207.84, -41) * mm});
            skLineSegment(sketch, "E370.1.0.0", {"start": v(-17, -22.36) * mm, "end": v(-17, -38) * mm});
            skPoint(sketch, "E370.1.0.1", {"position": v(-114.68, -41) * mm});
            skLineSegment(sketch, "E370.1.0.2", {"start": v(-85.18, -10.7) * mm, "end": v(-64.35, -36.1) * mm});
            skLineSegment(sketch, "E370.1.0.3", {"start": v(-47.43, -35.3) * mm, "end": v(-26.6, -9.9) * mm});
            skArc(sketch, "E370.1.0.4", {"start": v(-17, -22.36) * mm, "mid": v(-18.99, -19.53) * mm, "end": v(-22.32, -20.46) * mm});
            skPoint(sketch, "E370.1.0.5", {"position": v(-39.18, -41) * mm});
            skLineSegment(sketch, "E370.1.0.6", {"start": v(-70.59, -5) * mm, "end": v(-28.91, -5) * mm});
            skArc(sketch, "E370.1.0.7", {"start": v(-152.68, -20.46) * mm, "mid": v(-156.01, -19.53) * mm, "end": v(-158, -22.36) * mm});
            skPoint(sketch, "E370.1.0.8", {"position": v(-158, -41) * mm});
            skPoint(sketch, "E370.1.0.9", {"position": v(-17, -13.97) * mm});
            skPoint(sketch, "E370.1.0.10", {"position": v(-60.32, -41) * mm});
            skPoint(sketch, "E370.1.0.11", {"position": v(-98.07, -5) * mm});
            skPoint(sketch, "E370.1.0.12", {"position": v(-49.75, -38.12) * mm});
            skPoint(sketch, "E370.1.0.13", {"position": v(-125.25, -38.12) * mm});
            skPoint(sketch, "E370.1.0.14", {"position": v(-17, -41) * mm});
            skLineSegment(sketch, "E370.1.0.15", {"start": v(-122.93, -35.3) * mm, "end": v(-102.1, -9.9) * mm});
            skLineSegment(sketch, "E370.1.0.16", {"start": v(-72.9, -9.9) * mm, "end": v(-52.07, -35.3) * mm});
            skLineSegment(sketch, "E370.1.0.17", {"start": v(-108.34, -41) * mm, "end": v(-66.66, -41) * mm});
            skPoint(sketch, "E370.1.0.18", {"position": v(-76.93, -5) * mm});
            skPoint(sketch, "E370.1.0.19", {"position": v(-152.43, -5) * mm});
            skLineSegment(sketch, "E370.1.0.20", {"start": v(-35.15, -36.1) * mm, "end": v(-22.32, -20.46) * mm});
            skPoint(sketch, "E370.1.0.21", {"position": v(-158, -13.97) * mm});
            skPoint(sketch, "E370.1.0.22", {"position": v(-135.82, -41) * mm});
            skLineSegment(sketch, "E370.1.0.23", {"start": v(-152.68, -20.46) * mm, "end": v(-139.85, -36.1) * mm});
            skLineSegment(sketch, "E370.1.0.24", {"start": v(-158, -22.36) * mm, "end": v(-158, -38) * mm});
            skPoint(sketch, "E370.1.0.25", {"position": v(-22.57, -5) * mm});
            skLineSegment(sketch, "E370.1.0.26", {"start": v(-110.65, -36.1) * mm, "end": v(-89.82, -10.7) * mm});
            skLineSegment(sketch, "E370.1.0.27", {"start": v(-155, -41) * mm, "end": v(-142.16, -41) * mm});
            skLineSegment(sketch, "E370.1.0.28", {"start": v(-32.84, -41) * mm, "end": v(-20, -41) * mm});
            skPoint(sketch, "E370.1.0.29", {"position": v(-87.5, -7.88) * mm});
            skLineSegment(sketch, "E370.1.0.30", {"start": v(-146.09, -5) * mm, "end": v(-104.41, -5) * mm});
            skLineSegment(sketch, "E370.1.0.31", {"start": v(-148.4, -9.9) * mm, "end": v(-127.57, -35.3) * mm});
            skArc(sketch, "E370.1.0.32", {"start": v(-142.16, -41) * mm, "mid": v(-139.45, -39.28) * mm, "end": v(-139.85, -36.1) * mm});
            skArc(sketch, "E370.1.0.33", {"start": v(-146.09, -5) * mm, "mid": v(-148.8, -6.72) * mm, "end": v(-148.4, -9.9) * mm});
            skArc(sketch, "E370.1.0.34", {"start": v(-102.1, -9.9) * mm, "mid": v(-101.7, -6.72) * mm, "end": v(-104.41, -5) * mm});
            skArc(sketch, "E370.1.0.35", {"start": v(-26.6, -9.9) * mm, "mid": v(-26.2, -6.72) * mm, "end": v(-28.91, -5) * mm});
            skArc(sketch, "E370.1.0.36", {"start": v(-70.59, -5) * mm, "mid": v(-73.3, -6.72) * mm, "end": v(-72.9, -9.9) * mm});
            skArc(sketch, "E370.1.0.37", {"start": v(-35.15, -36.1) * mm, "mid": v(-35.55, -39.28) * mm, "end": v(-32.84, -41) * mm});
            skArc(sketch, "E370.1.0.38", {"start": v(-110.65, -36.1) * mm, "mid": v(-111.05, -39.28) * mm, "end": v(-108.34, -41) * mm});
            skArc(sketch, "E370.1.0.39", {"start": v(-66.66, -41) * mm, "mid": v(-63.95, -39.28) * mm, "end": v(-64.35, -36.1) * mm});
            skArc(sketch, "E370.1.0.40", {"start": v(-127.57, -35.3) * mm, "mid": v(-125.25, -36.39) * mm, "end": v(-122.93, -35.3) * mm});
            skArc(sketch, "E370.1.0.41", {"start": v(-52.07, -35.3) * mm, "mid": v(-49.75, -36.39) * mm, "end": v(-47.43, -35.3) * mm});
            skArc(sketch, "E370.1.0.42", {"start": v(-158, -38) * mm, "mid": v(-157.12, -40.12) * mm, "end": v(-155, -41) * mm});
            skArc(sketch, "E370.1.0.43", {"start": v(-85.18, -10.7) * mm, "mid": v(-87.5, -9.61) * mm, "end": v(-89.82, -10.7) * mm});
            skArc(sketch, "E370.1.0.44", {"start": v(-20, -41) * mm, "mid": v(-17.88, -40.12) * mm, "end": v(-17, -38) * mm});
            skLineSegment(sketch, "E370.1.0.45", {"start": v(-163, -46) * mm, "end": v(-125.25, -46) * mm, "construction": true});
            skLineSegment(sketch, "E370.direction1", {"start": v(-333, -41) * mm, "end": v(-158, -41) * mm, "construction": true});
            skSolve(sketch);
        }
        {
            var Q0;
            Q0 = qSketchRegion(id + "F17", true);
            extrude(context, id + "F18", {"entities" : qUnion([Q0]), "operationType" : NewBodyOperationType.REMOVE, "endBound" : BoundingType.THROUGH_ALL, "oppositeDirection" : true, "depth" : 25 * mm});
        }
        {
            var Q0;
            Q0=makeQuery(id+"F6.opExtrude","CAP_FACE",FACE,{"disambiguationData":[OSD([sQuery(id+"F5.wireOp",EDGE,"E96.0"),sQuery(id+"F5.wireOp",EDGE,"E97.0"),sQuery(id+"F5.wireOp",EDGE,"E98.0"),sQuery(id+"F5.wireOp",EDGE,"E99.0"),sQuery(id+"F5.wireOp",EDGE,"E100.0"),sQuery(id+"F5.wireOp",EDGE,"E101.0"),sQuery(id+"F5.wireOp",EDGE,"E102.0"),sQuery(id+"F5.wireOp",EDGE,"E103.0"),sQuery(id+"F5.wireOp",EDGE,"E104.0"),sQuery(id+"F5.wireOp",EDGE,"E105.0"),sQuery(id+"F5.wireOp",EDGE,"E106"),sQuery(id+"F5.wireOp",EDGE,"E107.1.0.0"),sQuery(id+"F5.wireOp",EDGE,"E107.2.0.0"),sQuery(id+"F5.wireOp",EDGE,"E109.0"),sQuery(id+"F5.wireOp",EDGE,"E110.0"),sQuery(id+"F5.wireOp",EDGE,"E111.0"),sQuery(id+"F5.wireOp",EDGE,"E112.0"),sQuery(id+"F5.wireOp",EDGE,"E112.1"),sQuery(id+"F5.wireOp",EDGE,"E112.2"),sQuery(id+"F5.wireOp",EDGE,"E112.3"),sQuery(id+"F5.wireOp",EDGE,"E113.MirrorC"),sQuery(id+"F5.wireOp",EDGE,"E114.MirrorC"),sQuery(id+"F5.wireOp",EDGE,"E115.MirrorC"),sQuery(id+"F5.wireOp",EDGE,"E116.MirrorC"),sQuery(id+"F5.wireOp",EDGE,"E117.MirrorC"),sQuery(id+"F5.wireOp",EDGE,"E118.MirrorC"),sQuery(id+"F5.wireOp",EDGE,"E119.MirrorC"),sQuery(id+"F5.wireOp",EDGE,"E120.MirrorCS"),sQuery(id+"F5.wireOp",EDGE,"E122.MirrorCS"),sQuery(id+"F5.wireOp",EDGE,"E123.MirrorCS"),sQuery(id+"F5.wireOp",EDGE,"E124.MirrorCS"),sQuery(id+"F5.wireOp",EDGE,"E125.MirrorCS"),sQuery(id+"F5.wireOp",EDGE,"E126.MirrorCS"),sQuery(id+"F5.wireOp",EDGE,"E127.MirrorCS"),sQuery(id+"F5.wireOp",EDGE,"E128.MirrorCS"),sQuery(id+"F5.wireOp",EDGE,"E129.MirrorCS"),sQuery(id+"F5.wireOp",EDGE,"E130.MirrorCS"),sQuery(id+"F5.wireOp",EDGE,"E132.MirrorCS")])],"isStart":false});
            var sketch = newSketch(context, id + "F19", { "sketchPlane" : qUnion([Q0])});
            skArc(sketch, "E371.0.0", {"start": v(-7.84, -4.53) * mm, "mid": v(0, -9.05) * mm, "end": v(7.84, -4.53) * mm});
            skLineSegment(sketch, "E371.0.1", {"start": v(7.84, -4.53) * mm, "end": v(22, 20) * mm});
            skLineSegment(sketch, "E371.0.2", {"start": v(22, 20) * mm, "end": v(22, 120) * mm});
            skLineSegment(sketch, "E371.0.3", {"start": v(22, 120) * mm, "end": v(7.84, 144.53) * mm});
            skArc(sketch, "E371.0.4", {"start": v(7.84, 144.53) * mm, "mid": v(0, 149.05) * mm, "end": v(-7.84, 144.53) * mm});
            skLineSegment(sketch, "E371.0.5", {"start": v(-7.84, 144.53) * mm, "end": v(-22, 120) * mm});
            skLineSegment(sketch, "E371.0.6", {"start": v(-22, 120) * mm, "end": v(-153, 120) * mm});
            skLineSegment(sketch, "E371.0.7", {"start": v(-153, 120) * mm, "end": v(-167.16, 144.53) * mm});
            skArc(sketch, "E371.0.8", {"start": v(-167.16, 144.53) * mm, "mid": v(-175, 149.05) * mm, "end": v(-182.84, 144.53) * mm});
            skLineSegment(sketch, "E371.0.9", {"start": v(-182.84, 144.53) * mm, "end": v(-197, 120) * mm});
            skLineSegment(sketch, "E371.0.10", {"start": v(-197, 120) * mm, "end": v(-328, 120) * mm});
            skLineSegment(sketch, "E371.0.11", {"start": v(-328, 120) * mm, "end": v(-342.16, 144.53) * mm});
            skArc(sketch, "E371.0.12", {"start": v(-342.16, 144.53) * mm, "mid": v(-350, 149.05) * mm, "end": v(-357.84, 144.53) * mm});
            skLineSegment(sketch, "E371.0.13", {"start": v(-357.84, 144.53) * mm, "end": v(-372, 120) * mm});
            skLineSegment(sketch, "E371.0.14", {"start": v(-372, 120) * mm, "end": v(-372, 20) * mm});
            skLineSegment(sketch, "E371.0.15", {"start": v(-372, 20) * mm, "end": v(-357.84, -4.53) * mm});
            skArc(sketch, "E371.0.16", {"start": v(-357.84, -4.53) * mm, "mid": v(-350, -9.05) * mm, "end": v(-342.16, -4.53) * mm});
            skLineSegment(sketch, "E371.0.17", {"start": v(-342.16, -4.53) * mm, "end": v(-328, 20) * mm});
            skLineSegment(sketch, "E371.0.18", {"start": v(-328, 20) * mm, "end": v(-197, 20) * mm});
            skLineSegment(sketch, "E371.0.19", {"start": v(-197, 20) * mm, "end": v(-182.84, -4.53) * mm});
            skArc(sketch, "E371.0.20", {"start": v(-182.84, -4.53) * mm, "mid": v(-175, -9.05) * mm, "end": v(-167.16, -4.53) * mm});
            skLineSegment(sketch, "E371.0.21", {"start": v(-167.16, -4.53) * mm, "end": v(-153, 20) * mm});
            skLineSegment(sketch, "E371.0.22", {"start": v(-153, 20) * mm, "end": v(-22, 20) * mm});
            skLineSegment(sketch, "E371.0.23", {"start": v(-22, 20) * mm, "end": v(-7.84, -4.53) * mm});
            skCircle(sketch, "E372.0", {"center": v(-67.5, 115) * mm, "radius": 1.5 * mm});
            skCircle(sketch, "E373.0", {"center": v(-107.5, 115) * mm, "radius": 1.5 * mm});
            skCircle(sketch, "E374.0", {"center": v(-242.5, 115) * mm, "radius": 1.5 * mm});
            skCircle(sketch, "E375.0", {"center": v(-282.5, 115) * mm, "radius": 1.5 * mm});
            skCircle(sketch, "E376.0", {"center": v(-282.5, 25) * mm, "radius": 1.5 * mm});
            skCircle(sketch, "E377.0", {"center": v(-242.5, 25) * mm, "radius": 1.5 * mm});
            skCircle(sketch, "E378.0", {"center": v(-107.5, 25) * mm, "radius": 1.5 * mm});
            skCircle(sketch, "E379.0", {"center": v(-67.5, 25) * mm, "radius": 1.5 * mm});
            skCircle(sketch, "E380.0", {"center": v(-350, 140) * mm, "radius": 1.5 * mm});
            skCircle(sketch, "E381.0", {"center": v(-175, 140) * mm, "radius": 1.5 * mm});
            skCircle(sketch, "E382.0", {"center": v(0, 140) * mm, "radius": 1.5 * mm});
            skCircle(sketch, "E383.0", {"center": v(0, 0) * mm, "radius": 1.5 * mm});
            skCircle(sketch, "E384.0", {"center": v(-175, 0) * mm, "radius": 1.5 * mm});
            skCircle(sketch, "E385.0", {"center": v(-350, 0) * mm, "radius": 1.5 * mm});
            skPoint(sketch, "E386.0", {"position": v(-355, 73) * mm});
            skPoint(sketch, "E387.0", {"position": v(-355, 67) * mm});
            skLineSegment(sketch, "E388", {"start": v(-355, 73) * mm, "end": v(-355, 67) * mm, "construction": true});
            skCircle(sketch, "E389", {"center": v(-355, 70) * mm, "radius": 1.5 * mm});
            skLineSegment(sketch, "E390.0.0", {"start": v(-318, 73) * mm, "end": v(-338, 73) * mm});
            skLineSegment(sketch, "E390.0.1", {"start": v(-338, 73) * mm, "end": v(-338, 67) * mm});
            skLineSegment(sketch, "E390.0.2", {"start": v(-338, 67) * mm, "end": v(-318, 67) * mm});
            skLineSegment(sketch, "E390.0.3", {"start": v(-318, 67) * mm, "end": v(-318, 73) * mm});
            skLineSegment(sketch, "E391.0.0", {"start": v(-187, 73) * mm, "end": v(-207, 73) * mm});
            skLineSegment(sketch, "E391.0.1", {"start": v(-207, 73) * mm, "end": v(-207, 67) * mm});
            skLineSegment(sketch, "E391.0.2", {"start": v(-207, 67) * mm, "end": v(-187, 67) * mm});
            skLineSegment(sketch, "E391.0.3", {"start": v(-187, 67) * mm, "end": v(-187, 73) * mm});
            skLineSegment(sketch, "E392.0.0", {"start": v(-143, 73) * mm, "end": v(-163, 73) * mm});
            skLineSegment(sketch, "E392.0.1", {"start": v(-163, 73) * mm, "end": v(-163, 67) * mm});
            skLineSegment(sketch, "E392.0.2", {"start": v(-163, 67) * mm, "end": v(-143, 67) * mm});
            skLineSegment(sketch, "E392.0.3", {"start": v(-143, 67) * mm, "end": v(-143, 73) * mm});
            skLineSegment(sketch, "E393.0.0", {"start": v(-12, 73) * mm, "end": v(-32, 73) * mm});
            skLineSegment(sketch, "E393.0.1", {"start": v(-32, 73) * mm, "end": v(-32, 67) * mm});
            skLineSegment(sketch, "E393.0.2", {"start": v(-32, 67) * mm, "end": v(-12, 67) * mm});
            skLineSegment(sketch, "E393.0.3", {"start": v(-12, 67) * mm, "end": v(-12, 73) * mm});
            skPoint(sketch, "E394.0", {"position": v(-175, 73) * mm});
            skPoint(sketch, "E395.0", {"position": v(-175, 67) * mm});
            skPoint(sketch, "E396.0", {"position": v(5, 73) * mm});
            skPoint(sketch, "E397.0", {"position": v(5, 67) * mm});
            skLineSegment(sketch, "E398", {"start": v(5, 73) * mm, "end": v(5, 67) * mm, "construction": true});
            skLineSegment(sketch, "E399", {"start": v(-175, 73) * mm, "end": v(-175, 67) * mm, "construction": true});
            skCircle(sketch, "E400", {"center": v(-175, 70) * mm, "radius": 1.5 * mm});
            skCircle(sketch, "E401", {"center": v(5, 70) * mm, "radius": 1.5 * mm});
            skCircle(sketch, "E402.0", {"center": v(-232, 82) * mm, "radius": 1.5 * mm});
            skCircle(sketch, "E403.0", {"center": v(-232, 58) * mm, "radius": 1.5 * mm});
            skCircle(sketch, "E404.0", {"center": v(-118, 58) * mm, "radius": 1.5 * mm});
            skCircle(sketch, "E405.0", {"center": v(-118, 82) * mm, "radius": 1.5 * mm});
            skSolve(sketch);
        }
        {
            var Q0;
            Q0=makeQuery(id+"F19.imprint","IMPRINT",FACE,{"disambiguationData":[TD([[makeQuery(id+"F19.imprint","IMPRINT",EDGE,{"derivedFrom":sQuery(id+"F19.wireOp",EDGE,"E389")}),1.0]])]});
            var Q1;
            Q1=makeQuery(id+"F19.imprint","IMPRINT",FACE,{"disambiguationData":[TD([[makeQuery(id+"F19.imprint","IMPRINT",EDGE,{"derivedFrom":sQuery(id+"F19.wireOp",EDGE,"E400")}),1.0]])]});
            var Q2;
            Q2=makeQuery(id+"F19.imprint","IMPRINT",FACE,{"disambiguationData":[TD([[makeQuery(id+"F19.imprint","IMPRINT",EDGE,{"derivedFrom":sQuery(id+"F19.wireOp",EDGE,"E401")}),1.0]])]});
            extrude(context, id + "F20", {"entities" : qUnion([Q0, Q1, Q2]), "operationType" : NewBodyOperationType.REMOVE, "endBound" : BoundingType.UP_TO_NEXT, "oppositeDirection" : true, "depth" : 25 * mm});
        }
    });
